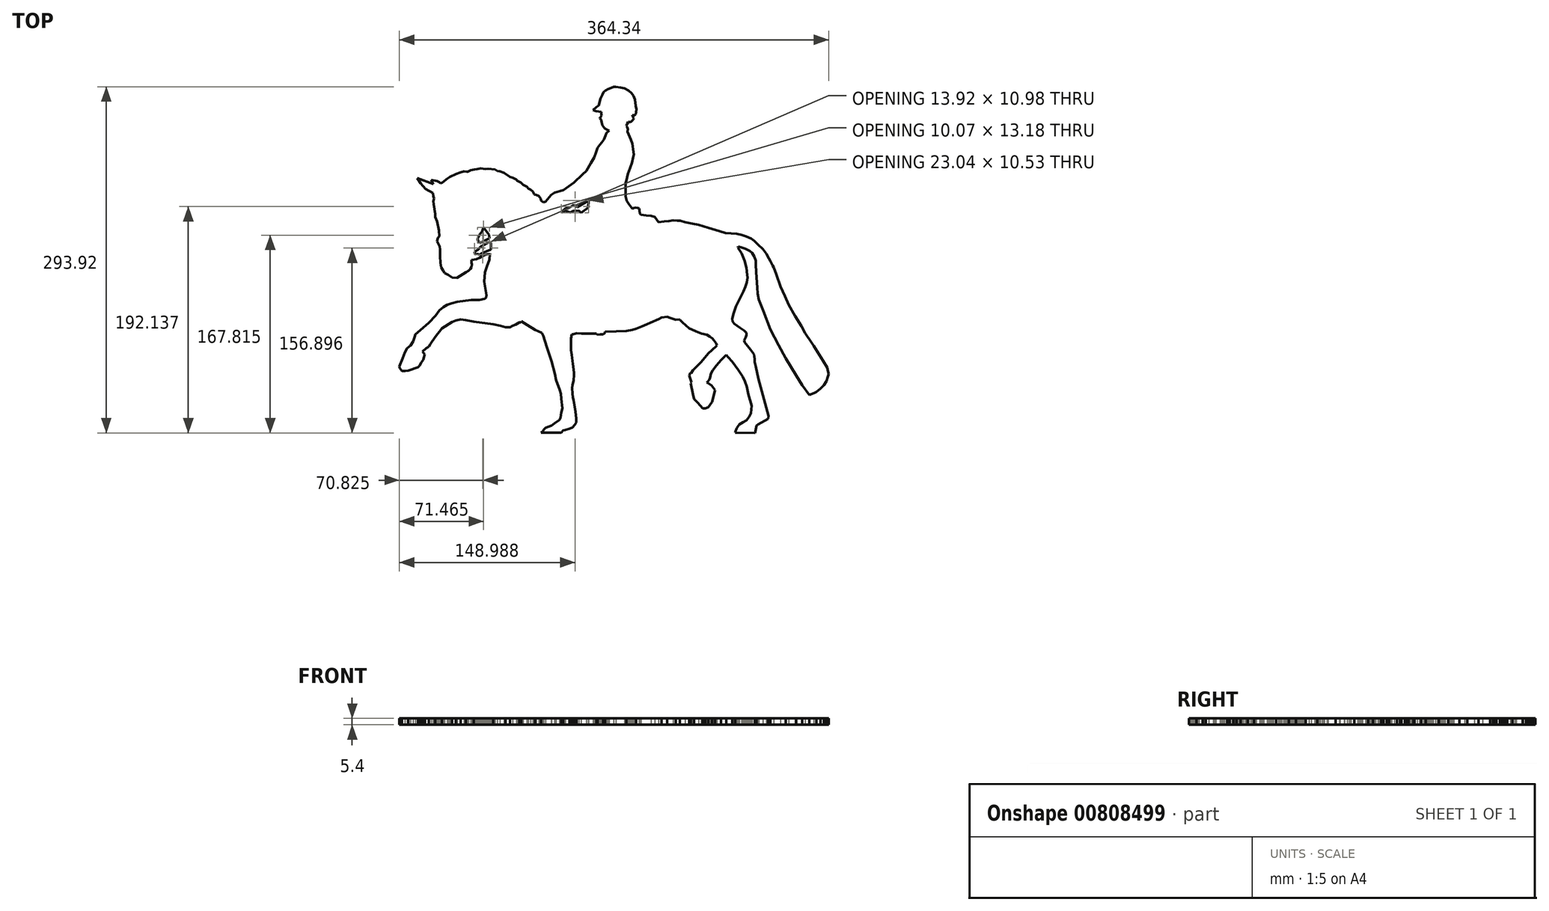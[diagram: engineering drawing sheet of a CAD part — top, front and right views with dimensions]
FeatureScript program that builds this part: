
annotation { "Feature Type Name" : "Feature", "Feature Type Description" : "" }
export const myFeature = defineFeature(function(context is Context, id is Id, definition is map)
    precondition{}
    {
        {
            var Q0;
            Q0=qCreatedBy(makeId("Top.planeOp"),FACE);
            var sketch = newSketch(context, id + "F0", { "sketchPlane" : qUnion([Q0])});
            skLineSegment(sketch, "E0", {"start": v(-15.37, 154) * mm, "end": v(-13.56, 161.2) * mm});
            skLineSegment(sketch, "E1", {"start": v(-13.56, 161.2) * mm, "end": v(-11.74, 164.95) * mm});
            skLineSegment(sketch, "E2", {"start": v(-11.74, 164.95) * mm, "end": v(-10.33, 167.52) * mm});
            skLineSegment(sketch, "E3", {"start": v(-10.33, 167.52) * mm, "end": v(-8.43, 168.95) * mm});
            skLineSegment(sketch, "E4", {"start": v(-8.43, 168.95) * mm, "end": v(-6.07, 170.71) * mm});
            skLineSegment(sketch, "E5", {"start": v(-6.07, 170.71) * mm, "end": v(-3.07, 171.86) * mm});
            skLineSegment(sketch, "E6", {"start": v(-3.07, 171.86) * mm, "end": v(-0.38, 172.9) * mm});
            skLineSegment(sketch, "E7", {"start": v(-0.38, 172.9) * mm, "end": v(1.87, 172.9) * mm});
            skLineSegment(sketch, "E8", {"start": v(1.87, 172.9) * mm, "end": v(6.63, 171.98) * mm});
            skLineSegment(sketch, "E9", {"start": v(6.63, 171.98) * mm, "end": v(10.5, 171.24) * mm});
            skLineSegment(sketch, "E10", {"start": v(10.5, 171.24) * mm, "end": v(14.63, 169.07) * mm});
            skLineSegment(sketch, "E11", {"start": v(14.63, 169.07) * mm, "end": v(17.67, 166.4) * mm});
            skLineSegment(sketch, "E12", {"start": v(17.67, 166.4) * mm, "end": v(19.46, 163.77) * mm});
            skLineSegment(sketch, "E13", {"start": v(19.46, 163.77) * mm, "end": v(20.82, 160.15) * mm});
            skLineSegment(sketch, "E14", {"start": v(20.82, 160.15) * mm, "end": v(21.78, 153.95) * mm});
            skLineSegment(sketch, "E15", {"start": v(21.78, 153.95) * mm, "end": v(22.35, 150.26) * mm});
            skLineSegment(sketch, "E16", {"start": v(22.35, 150.26) * mm, "end": v(21.66, 145.02) * mm});
            skLineSegment(sketch, "E17", {"start": v(21.66, 145.02) * mm, "end": v(20.23, 144.3) * mm});
            skLineSegment(sketch, "E18", {"start": v(20.23, 144.3) * mm, "end": v(18.45, 144.3) * mm});
            skLineSegment(sketch, "E19", {"start": v(18.45, 144.3) * mm, "end": v(18.45, 143.54) * mm});
            skLineSegment(sketch, "E20", {"start": v(18.45, 143.54) * mm, "end": v(19.7, 141.63) * mm});
            skLineSegment(sketch, "E21", {"start": v(19.7, 141.63) * mm, "end": v(18.86, 139.85) * mm});
            skLineSegment(sketch, "E22", {"start": v(18.86, 139.85) * mm, "end": v(17.08, 138) * mm});
            skLineSegment(sketch, "E23", {"start": v(17.08, 138) * mm, "end": v(16.05, 137.61) * mm});
            skLineSegment(sketch, "E24", {"start": v(16.05, 137.61) * mm, "end": v(14.06, 137.61) * mm});
            skLineSegment(sketch, "E25", {"start": v(14.06, 137.61) * mm, "end": v(13.19, 135.72) * mm});
            skLineSegment(sketch, "E26", {"start": v(13.19, 135.72) * mm, "end": v(12.47, 134.16) * mm});
            skLineSegment(sketch, "E27", {"start": v(12.47, 134.16) * mm, "end": v(13.23, 133) * mm});
            skLineSegment(sketch, "E28", {"start": v(13.23, 133) * mm, "end": v(13.7, 130.65) * mm});
            skLineSegment(sketch, "E29", {"start": v(13.7, 130.65) * mm, "end": v(13.45, 127.94) * mm});
            skLineSegment(sketch, "E30", {"start": v(13.45, 127.94) * mm, "end": v(14.48, 125.44) * mm});
            skLineSegment(sketch, "E31", {"start": v(14.48, 125.44) * mm, "end": v(16.64, 120.14) * mm});
            skLineSegment(sketch, "E32", {"start": v(16.64, 120.14) * mm, "end": v(18.28, 116.14) * mm});
            skLineSegment(sketch, "E33", {"start": v(18.28, 116.14) * mm, "end": v(18.93, 111.56) * mm});
            skLineSegment(sketch, "E34", {"start": v(18.93, 111.56) * mm, "end": v(19.48, 107.66) * mm});
            skLineSegment(sketch, "E35", {"start": v(19.48, 107.66) * mm, "end": v(19.84, 105.1) * mm});
            skLineSegment(sketch, "E36", {"start": v(19.84, 105.1) * mm, "end": v(19.12, 102.22) * mm});
            skLineSegment(sketch, "E37", {"start": v(19.12, 102.22) * mm, "end": v(17.84, 97.06) * mm});
            skLineSegment(sketch, "E38", {"start": v(17.84, 97.06) * mm, "end": v(15.94, 91.85) * mm});
            skLineSegment(sketch, "E39", {"start": v(15.94, 91.85) * mm, "end": v(13.76, 85.9) * mm});
            skLineSegment(sketch, "E40", {"start": v(13.76, 85.9) * mm, "end": v(12.23, 79.26) * mm});
            skLineSegment(sketch, "E41", {"start": v(12.23, 79.26) * mm, "end": v(11.64, 76.7) * mm});
            skLineSegment(sketch, "E42", {"start": v(11.64, 76.7) * mm, "end": v(11.64, 68.11) * mm});
            skLineSegment(sketch, "E43", {"start": v(11.64, 68.11) * mm, "end": v(11.64, 66.83) * mm});
            skLineSegment(sketch, "E44", {"start": v(11.64, 66.83) * mm, "end": v(11.64, 63.5) * mm});
            skLineSegment(sketch, "E45", {"start": v(11.64, 63.5) * mm, "end": v(12.53, 59.03) * mm});
            skLineSegment(sketch, "E46", {"start": v(12.53, 59.03) * mm, "end": v(14.96, 55.61) * mm});
            skLineSegment(sketch, "E47", {"start": v(14.96, 55.61) * mm, "end": v(18.15, 51.12) * mm});
            skLineSegment(sketch, "E48", {"start": v(18.15, 51.12) * mm, "end": v(19.88, 51.64) * mm});
            skLineSegment(sketch, "E49", {"start": v(19.88, 51.64) * mm, "end": v(21.8, 52.22) * mm});
            skLineSegment(sketch, "E50", {"start": v(21.8, 52.22) * mm, "end": v(23.75, 51.69) * mm});
            skLineSegment(sketch, "E51", {"start": v(23.75, 51.69) * mm, "end": v(25.12, 51.32) * mm});
            skLineSegment(sketch, "E52", {"start": v(25.12, 51.32) * mm, "end": v(25.29, 49.75) * mm});
            skLineSegment(sketch, "E53", {"start": v(25.29, 49.75) * mm, "end": v(25.65, 46.4) * mm});
            skLineSegment(sketch, "E54", {"start": v(25.65, 46.4) * mm, "end": v(26.93, 45.03) * mm});
            skLineSegment(sketch, "E55", {"start": v(26.93, 45.03) * mm, "end": v(31.94, 44.43) * mm});
            skLineSegment(sketch, "E56", {"start": v(31.94, 44.43) * mm, "end": v(37.06, 43.83) * mm});
            skLineSegment(sketch, "E57", {"start": v(37.06, 43.83) * mm, "end": v(40.68, 42.7) * mm});
            skLineSegment(sketch, "E58", {"start": v(40.68, 42.7) * mm, "end": v(42.57, 40.2) * mm});
            skLineSegment(sketch, "E59", {"start": v(42.57, 40.2) * mm, "end": v(44.49, 37.67) * mm});
            skLineSegment(sketch, "E60", {"start": v(44.49, 37.67) * mm, "end": v(50.12, 38.31) * mm});
            skLineSegment(sketch, "E61", {"start": v(50.12, 38.31) * mm, "end": v(54.89, 38.86) * mm});
            skLineSegment(sketch, "E62", {"start": v(54.89, 38.86) * mm, "end": v(58.92, 39.32) * mm});
            skLineSegment(sketch, "E63", {"start": v(58.92, 39.32) * mm, "end": v(63.15, 39.2) * mm});
            skLineSegment(sketch, "E64", {"start": v(63.15, 39.2) * mm, "end": v(66.23, 39.12) * mm});
            skLineSegment(sketch, "E65", {"start": v(66.23, 39.12) * mm, "end": v(71, 37.71) * mm});
            skLineSegment(sketch, "E66", {"start": v(71, 37.71) * mm, "end": v(78.25, 36.22) * mm});
            skLineSegment(sketch, "E67", {"start": v(78.25, 36.22) * mm, "end": v(84.31, 34.97) * mm});
            skLineSegment(sketch, "E68", {"start": v(84.31, 34.97) * mm, "end": v(94, 32.04) * mm});
            skLineSegment(sketch, "E69", {"start": v(94, 32.04) * mm, "end": v(105.26, 28.65) * mm});
            skLineSegment(sketch, "E70", {"start": v(105.26, 28.65) * mm, "end": v(111.22, 26.85) * mm});
            skLineSegment(sketch, "E71", {"start": v(111.22, 26.85) * mm, "end": v(116.82, 26.42) * mm});
            skLineSegment(sketch, "E72", {"start": v(116.82, 26.42) * mm, "end": v(122.43, 26) * mm});
            skLineSegment(sketch, "E73", {"start": v(122.43, 26) * mm, "end": v(127.42, 24.88) * mm});
            skLineSegment(sketch, "E74", {"start": v(127.42, 24.88) * mm, "end": v(131.84, 23.24) * mm});
            skLineSegment(sketch, "E75", {"start": v(131.84, 23.24) * mm, "end": v(137.18, 21.26) * mm});
            skLineSegment(sketch, "E76", {"start": v(137.18, 21.26) * mm, "end": v(140.13, 19.07) * mm});
            skLineSegment(sketch, "E77", {"start": v(140.13, 19.07) * mm, "end": v(143.87, 15.4) * mm});
            skLineSegment(sketch, "E78", {"start": v(143.87, 15.4) * mm, "end": v(148.55, 10.79) * mm});
            skLineSegment(sketch, "E79", {"start": v(148.55, 10.79) * mm, "end": v(151.92, 6.2) * mm});
            skLineSegment(sketch, "E80", {"start": v(151.92, 6.2) * mm, "end": v(154.55, 1.43) * mm});
            skLineSegment(sketch, "E81", {"start": v(154.55, 1.43) * mm, "end": v(156.03, -1.24) * mm});
            skLineSegment(sketch, "E82", {"start": v(156.03, -1.24) * mm, "end": v(158.45, -5.64) * mm});
            skLineSegment(sketch, "E83", {"start": v(158.45, -5.64) * mm, "end": v(159.57, -7.67) * mm});
            skLineSegment(sketch, "E84", {"start": v(159.57, -7.67) * mm, "end": v(162, -14.62) * mm});
            skLineSegment(sketch, "E85", {"start": v(162, -14.62) * mm, "end": v(166.17, -26.5) * mm});
            skLineSegment(sketch, "E86", {"start": v(166.17, -26.5) * mm, "end": v(170.5, -36.2) * mm});
            skLineSegment(sketch, "E87", {"start": v(170.5, -36.2) * mm, "end": v(174.36, -44.8) * mm});
            skLineSegment(sketch, "E88", {"start": v(174.36, -44.8) * mm, "end": v(180.75, -56.32) * mm});
            skLineSegment(sketch, "E89", {"start": v(180.75, -56.32) * mm, "end": v(187, -66.21) * mm});
            skLineSegment(sketch, "E90", {"start": v(187, -66.21) * mm, "end": v(191.02, -73.19) * mm});
            skLineSegment(sketch, "E91", {"start": v(191.02, -73.19) * mm, "end": v(197.28, -82.58) * mm});
            skLineSegment(sketch, "E92", {"start": v(197.28, -82.58) * mm, "end": v(199.58, -86.03) * mm});
            skLineSegment(sketch, "E93", {"start": v(199.58, -86.03) * mm, "end": v(208.64, -100.87) * mm});
            skLineSegment(sketch, "E94", {"start": v(208.64, -100.87) * mm, "end": v(212.88, -107.8) * mm});
            skLineSegment(sketch, "E95", {"start": v(212.88, -107.8) * mm, "end": v(213.74, -111.58) * mm});
            skLineSegment(sketch, "E96", {"start": v(213.74, -111.58) * mm, "end": v(214.31, -114.1) * mm});
            skLineSegment(sketch, "E97", {"start": v(214.31, -114.1) * mm, "end": v(213.22, -117.4) * mm});
            skLineSegment(sketch, "E98", {"start": v(213.22, -117.4) * mm, "end": v(211.97, -121.16) * mm});
            skLineSegment(sketch, "E99", {"start": v(211.97, -121.16) * mm, "end": v(209.44, -125.28) * mm});
            skLineSegment(sketch, "E100", {"start": v(209.44, -125.28) * mm, "end": v(206.32, -128.57) * mm});
            skLineSegment(sketch, "E101", {"start": v(206.32, -128.57) * mm, "end": v(202.14, -132.05) * mm});
            skLineSegment(sketch, "E102", {"start": v(202.14, -132.05) * mm, "end": v(199.85, -132.94) * mm});
            skLineSegment(sketch, "E103", {"start": v(199.85, -132.94) * mm, "end": v(194.97, -134.81) * mm});
            skLineSegment(sketch, "E104", {"start": v(194.97, -134.81) * mm, "end": v(187.9, -125.23) * mm});
            skLineSegment(sketch, "E105", {"start": v(187.9, -125.23) * mm, "end": v(181.73, -115.6) * mm});
            skLineSegment(sketch, "E106", {"start": v(181.73, -115.6) * mm, "end": v(171.37, -98.23) * mm});
            skLineSegment(sketch, "E107", {"start": v(171.37, -98.23) * mm, "end": v(164.42, -85.16) * mm});
            skLineSegment(sketch, "E108", {"start": v(164.42, -85.16) * mm, "end": v(156.13, -69.55) * mm});
            skLineSegment(sketch, "E109", {"start": v(156.13, -69.55) * mm, "end": v(148.82, -51.07) * mm});
            skLineSegment(sketch, "E110", {"start": v(148.82, -51.07) * mm, "end": v(144.38, -39.85) * mm});
            skLineSegment(sketch, "E111", {"start": v(144.38, -39.85) * mm, "end": v(143.29, -33.88) * mm});
            skLineSegment(sketch, "E112", {"start": v(143.29, -33.88) * mm, "end": v(142.93, -27.82) * mm});
            skLineSegment(sketch, "E113", {"start": v(142.93, -27.82) * mm, "end": v(142.04, -12.48) * mm});
            skLineSegment(sketch, "E114", {"start": v(142.04, -12.48) * mm, "end": v(141.59, -4.76) * mm});
            skLineSegment(sketch, "E115", {"start": v(141.59, -4.76) * mm, "end": v(141.37, -0.93) * mm});
            skLineSegment(sketch, "E116", {"start": v(141.37, -0.93) * mm, "end": v(140.11, 3.27) * mm});
            skLineSegment(sketch, "E117", {"start": v(140.11, 3.27) * mm, "end": v(137.82, 7.09) * mm});
            skLineSegment(sketch, "E118", {"start": v(137.82, 7.09) * mm, "end": v(135.57, 8.99) * mm});
            skLineSegment(sketch, "E119", {"start": v(135.57, 8.99) * mm, "end": v(130.99, 11.28) * mm});
            skLineSegment(sketch, "E120", {"start": v(130.99, 11.28) * mm, "end": v(126.7, 12.63) * mm});
            skLineSegment(sketch, "E121", {"start": v(126.7, 12.63) * mm, "end": v(124.1, 13.45) * mm});
            skLineSegment(sketch, "E122", {"start": v(124.1, 13.45) * mm, "end": v(123.63, 12.16) * mm});
            skLineSegment(sketch, "E123", {"start": v(123.63, 12.16) * mm, "end": v(125.05, 10.1) * mm});
            skLineSegment(sketch, "E124", {"start": v(125.05, 10.1) * mm, "end": v(127.45, 6.6) * mm});
            skLineSegment(sketch, "E125", {"start": v(127.45, 6.6) * mm, "end": v(128.99, 2.87) * mm});
            skLineSegment(sketch, "E126", {"start": v(128.99, 2.87) * mm, "end": v(130.5, -0.81) * mm});
            skLineSegment(sketch, "E127", {"start": v(130.5, -0.81) * mm, "end": v(132.22, -7.94) * mm});
            skLineSegment(sketch, "E128", {"start": v(132.22, -7.94) * mm, "end": v(133.05, -14.95) * mm});
            skLineSegment(sketch, "E129", {"start": v(133.05, -14.95) * mm, "end": v(133.36, -17.62) * mm});
            skLineSegment(sketch, "E130", {"start": v(133.36, -17.62) * mm, "end": v(132.75, -22.6) * mm});
            skLineSegment(sketch, "E131", {"start": v(132.75, -22.6) * mm, "end": v(131.22, -27.13) * mm});
            skLineSegment(sketch, "E132", {"start": v(131.22, -27.13) * mm, "end": v(129.1, -31.42) * mm});
            skLineSegment(sketch, "E133", {"start": v(129.1, -31.42) * mm, "end": v(124.58, -40.6) * mm});
            skLineSegment(sketch, "E134", {"start": v(124.58, -40.6) * mm, "end": v(121.74, -46.35) * mm});
            skLineSegment(sketch, "E135", {"start": v(121.74, -46.35) * mm, "end": v(119.4, -52.99) * mm});
            skLineSegment(sketch, "E136", {"start": v(119.4, -52.99) * mm, "end": v(118.1, -58.57) * mm});
            skLineSegment(sketch, "E137", {"start": v(118.1, -58.57) * mm, "end": v(118.33, -61.75) * mm});
            skLineSegment(sketch, "E138", {"start": v(118.33, -61.75) * mm, "end": v(120.16, -64.16) * mm});
            skLineSegment(sketch, "E139", {"start": v(120.16, -64.16) * mm, "end": v(125.63, -67.71) * mm});
            skLineSegment(sketch, "E140", {"start": v(125.63, -67.71) * mm, "end": v(129.97, -70.52) * mm});
            skLineSegment(sketch, "E141", {"start": v(129.97, -70.52) * mm, "end": v(132.04, -72.94) * mm});
            skLineSegment(sketch, "E142", {"start": v(132.04, -72.94) * mm, "end": v(132.34, -75.24) * mm});
            skLineSegment(sketch, "E143", {"start": v(132.34, -75.24) * mm, "end": v(131.28, -77.53) * mm});
            skLineSegment(sketch, "E144", {"start": v(131.28, -77.53) * mm, "end": v(130.02, -80.26) * mm});
            skLineSegment(sketch, "E145", {"start": v(130.02, -80.26) * mm, "end": v(130.4, -82.25) * mm});
            skLineSegment(sketch, "E146", {"start": v(130.4, -82.25) * mm, "end": v(136.34, -89.84) * mm});
            skLineSegment(sketch, "E147", {"start": v(136.34, -89.84) * mm, "end": v(139.78, -94.23) * mm});
            skLineSegment(sketch, "E148", {"start": v(139.78, -94.23) * mm, "end": v(140.16, -96.48) * mm});
            skLineSegment(sketch, "E149", {"start": v(140.16, -96.48) * mm, "end": v(140.6, -99) * mm});
            skLineSegment(sketch, "E150", {"start": v(140.6, -99) * mm, "end": v(140.4, -102.03) * mm});
            skLineSegment(sketch, "E151", {"start": v(140.4, -102.03) * mm, "end": v(141.4, -106.38) * mm});
            skLineSegment(sketch, "E152", {"start": v(141.4, -106.38) * mm, "end": v(144.26, -118.83) * mm});
            skLineSegment(sketch, "E153", {"start": v(144.26, -118.83) * mm, "end": v(148.7, -135.34) * mm});
            skLineSegment(sketch, "E154", {"start": v(148.7, -135.34) * mm, "end": v(152.32, -148.84) * mm});
            skLineSegment(sketch, "E155", {"start": v(152.32, -148.84) * mm, "end": v(154.25, -156) * mm});
            skLineSegment(sketch, "E156", {"start": v(154.25, -156) * mm, "end": v(153.94, -158.96) * mm});
            skLineSegment(sketch, "E157", {"start": v(153.94, -158.96) * mm, "end": v(143.88, -164.55) * mm});
            skLineSegment(sketch, "E158", {"start": v(143.88, -164.55) * mm, "end": v(142.23, -165.47) * mm});
            skLineSegment(sketch, "E159", {"start": v(142.23, -165.47) * mm, "end": v(141.65, -168.66) * mm});
            skLineSegment(sketch, "E160", {"start": v(141.65, -168.66) * mm, "end": v(140.88, -172.9) * mm});
            skLineSegment(sketch, "E161", {"start": v(140.88, -172.9) * mm, "end": v(120.98, -172.74) * mm});
            skLineSegment(sketch, "E162", {"start": v(120.98, -172.74) * mm, "end": v(121.45, -171.15) * mm});
            skLineSegment(sketch, "E163", {"start": v(121.45, -171.15) * mm, "end": v(122.31, -168.25) * mm});
            skLineSegment(sketch, "E164", {"start": v(122.31, -168.25) * mm, "end": v(124.04, -165.86) * mm});
            skLineSegment(sketch, "E165", {"start": v(124.04, -165.86) * mm, "end": v(125.1, -164.4) * mm});
            skLineSegment(sketch, "E166", {"start": v(125.1, -164.4) * mm, "end": v(128.8, -162.28) * mm});
            skLineSegment(sketch, "E167", {"start": v(128.8, -162.28) * mm, "end": v(132.28, -160.28) * mm});
            skLineSegment(sketch, "E168", {"start": v(132.28, -160.28) * mm, "end": v(134.8, -157.04) * mm});
            skLineSegment(sketch, "E169", {"start": v(134.8, -157.04) * mm, "end": v(136.63, -153.16) * mm});
            skLineSegment(sketch, "E170", {"start": v(136.63, -153.16) * mm, "end": v(137.04, -149.7) * mm});
            skLineSegment(sketch, "E171", {"start": v(137.04, -149.7) * mm, "end": v(137.49, -145.93) * mm});
            skLineSegment(sketch, "E172", {"start": v(137.49, -145.93) * mm, "end": v(133.92, -134.1) * mm});
            skLineSegment(sketch, "E173", {"start": v(133.92, -134.1) * mm, "end": v(132.74, -126.6) * mm});
            skLineSegment(sketch, "E174", {"start": v(132.74, -126.6) * mm, "end": v(130.8, -121.43) * mm});
            skLineSegment(sketch, "E175", {"start": v(130.8, -121.43) * mm, "end": v(128.33, -116.78) * mm});
            skLineSegment(sketch, "E176", {"start": v(128.33, -116.78) * mm, "end": v(123.8, -110.01) * mm});
            skLineSegment(sketch, "E177", {"start": v(123.8, -110.01) * mm, "end": v(118.14, -101.57) * mm});
            skLineSegment(sketch, "E178", {"start": v(118.14, -101.57) * mm, "end": v(114.02, -97.18) * mm});
            skLineSegment(sketch, "E179", {"start": v(114.02, -97.18) * mm, "end": v(111.93, -94.95) * mm});
            skLineSegment(sketch, "E180", {"start": v(111.93, -94.95) * mm, "end": v(106.73, -100.05) * mm});
            skLineSegment(sketch, "E181", {"start": v(106.73, -100.05) * mm, "end": v(102.5, -105.4) * mm});
            skLineSegment(sketch, "E182", {"start": v(102.5, -105.4) * mm, "end": v(98.67, -110.22) * mm});
            skLineSegment(sketch, "E183", {"start": v(98.67, -110.22) * mm, "end": v(96.79, -113.8) * mm});
            skLineSegment(sketch, "E184", {"start": v(96.79, -113.8) * mm, "end": v(95.9, -117.4) * mm});
            skLineSegment(sketch, "E185", {"start": v(95.9, -117.4) * mm, "end": v(95.33, -119.72) * mm});
            skLineSegment(sketch, "E186", {"start": v(95.33, -119.72) * mm, "end": v(93.38, -121.92) * mm});
            skLineSegment(sketch, "E187", {"start": v(93.38, -121.92) * mm, "end": v(92.71, -122.66) * mm});
            skLineSegment(sketch, "E188", {"start": v(92.71, -122.66) * mm, "end": v(93.67, -123.1) * mm});
            skLineSegment(sketch, "E189", {"start": v(93.67, -123.1) * mm, "end": v(97.32, -125.63) * mm});
            skLineSegment(sketch, "E190", {"start": v(97.32, -125.63) * mm, "end": v(99.61, -128.52) * mm});
            skLineSegment(sketch, "E191", {"start": v(99.61, -128.52) * mm, "end": v(100.78, -129.98) * mm});
            skLineSegment(sketch, "E192", {"start": v(100.78, -129.98) * mm, "end": v(98.5, -139.47) * mm});
            skLineSegment(sketch, "E193", {"start": v(98.5, -139.47) * mm, "end": v(97.92, -141.87) * mm});
            skLineSegment(sketch, "E194", {"start": v(97.92, -141.87) * mm, "end": v(95.9, -144.72) * mm});
            skLineSegment(sketch, "E195", {"start": v(95.9, -144.72) * mm, "end": v(93.95, -147.46) * mm});
            skLineSegment(sketch, "E196", {"start": v(93.95, -147.46) * mm, "end": v(91.07, -148.36) * mm});
            skLineSegment(sketch, "E197", {"start": v(91.07, -148.36) * mm, "end": v(88.54, -148.3) * mm});
            skLineSegment(sketch, "E198", {"start": v(88.54, -148.3) * mm, "end": v(86.19, -145.77) * mm});
            skLineSegment(sketch, "E199", {"start": v(86.19, -145.77) * mm, "end": v(83.23, -142.6) * mm});
            skLineSegment(sketch, "E200", {"start": v(83.23, -142.6) * mm, "end": v(81.22, -140.42) * mm});
            skLineSegment(sketch, "E201", {"start": v(81.22, -140.42) * mm, "end": v(80.8, -139.99) * mm});
            skLineSegment(sketch, "E202", {"start": v(80.8, -139.99) * mm, "end": v(79.96, -139.08) * mm});
            skLineSegment(sketch, "E203", {"start": v(79.96, -139.08) * mm, "end": v(78.88, -134.06) * mm});
            skLineSegment(sketch, "E204", {"start": v(78.88, -134.06) * mm, "end": v(76.6, -123.46) * mm});
            skLineSegment(sketch, "E205", {"start": v(76.6, -123.46) * mm, "end": v(77.12, -122.25) * mm});
            skLineSegment(sketch, "E206", {"start": v(77.12, -122.25) * mm, "end": v(75.18, -115.66) * mm});
            skLineSegment(sketch, "E207", {"start": v(75.18, -115.66) * mm, "end": v(75.65, -114.13) * mm});
            skLineSegment(sketch, "E208", {"start": v(75.65, -114.13) * mm, "end": v(75.98, -113.05) * mm});
            skLineSegment(sketch, "E209", {"start": v(75.98, -113.05) * mm, "end": v(76.83, -113.13) * mm});
            skLineSegment(sketch, "E210", {"start": v(76.83, -113.13) * mm, "end": v(78.94, -110.31) * mm});
            skLineSegment(sketch, "E211", {"start": v(78.94, -110.31) * mm, "end": v(86.95, -102.12) * mm});
            skLineSegment(sketch, "E212", {"start": v(86.95, -102.12) * mm, "end": v(94.24, -93.65) * mm});
            skLineSegment(sketch, "E213", {"start": v(94.24, -93.65) * mm, "end": v(101.78, -86.28) * mm});
            skLineSegment(sketch, "E214", {"start": v(101.78, -86.28) * mm, "end": v(102.67, -85.4) * mm});
            skLineSegment(sketch, "E215", {"start": v(102.67, -85.4) * mm, "end": v(101.95, -83.51) * mm});
            skLineSegment(sketch, "E216", {"start": v(101.95, -83.51) * mm, "end": v(99.78, -80.52) * mm});
            skLineSegment(sketch, "E217", {"start": v(99.78, -80.52) * mm, "end": v(98.27, -78.44) * mm});
            skLineSegment(sketch, "E218", {"start": v(98.27, -78.44) * mm, "end": v(95.42, -76.68) * mm});
            skLineSegment(sketch, "E219", {"start": v(95.42, -76.68) * mm, "end": v(92.65, -74.98) * mm});
            skLineSegment(sketch, "E220", {"start": v(92.65, -74.98) * mm, "end": v(87.24, -73.68) * mm});
            skLineSegment(sketch, "E221", {"start": v(87.24, -73.68) * mm, "end": v(81.89, -71.45) * mm});
            skLineSegment(sketch, "E222", {"start": v(81.89, -71.45) * mm, "end": v(77.64, -69.67) * mm});
            skLineSegment(sketch, "E223", {"start": v(77.64, -69.67) * mm, "end": v(74.96, -68.56) * mm});
            skLineSegment(sketch, "E224", {"start": v(74.96, -68.56) * mm, "end": v(68.4, -62.32) * mm});
            skLineSegment(sketch, "E225", {"start": v(68.4, -62.32) * mm, "end": v(66.26, -60.27) * mm});
            skLineSegment(sketch, "E226", {"start": v(66.26, -60.27) * mm, "end": v(65.57, -59.62) * mm});
            skLineSegment(sketch, "E227", {"start": v(65.57, -59.62) * mm, "end": v(61.7, -59.84) * mm});
            skLineSegment(sketch, "E228", {"start": v(61.7, -59.84) * mm, "end": v(55.87, -57.85) * mm});
            skLineSegment(sketch, "E229", {"start": v(55.87, -57.85) * mm, "end": v(53.16, -56.91) * mm});
            skLineSegment(sketch, "E230", {"start": v(53.16, -56.91) * mm, "end": v(47.57, -57.78) * mm});
            skLineSegment(sketch, "E231", {"start": v(47.57, -57.78) * mm, "end": v(44.63, -59.07) * mm});
            skLineSegment(sketch, "E232", {"start": v(44.63, -59.07) * mm, "end": v(36.37, -62.7) * mm});
            skLineSegment(sketch, "E233", {"start": v(36.37, -62.7) * mm, "end": v(32.94, -64.21) * mm});
            skLineSegment(sketch, "E234", {"start": v(32.94, -64.21) * mm, "end": v(27.77, -66.49) * mm});
            skLineSegment(sketch, "E235", {"start": v(27.77, -66.49) * mm, "end": v(22.08, -68.99) * mm});
            skLineSegment(sketch, "E236", {"start": v(22.08, -68.99) * mm, "end": v(18.2, -69.84) * mm});
            skLineSegment(sketch, "E237", {"start": v(18.2, -69.84) * mm, "end": v(12.42, -71.11) * mm});
            skLineSegment(sketch, "E238", {"start": v(12.42, -71.11) * mm, "end": v(2.3, -71.5) * mm});
            skLineSegment(sketch, "E239", {"start": v(2.3, -71.5) * mm, "end": v(-9.07, -71.92) * mm});
            skLineSegment(sketch, "E240", {"start": v(-9.07, -71.92) * mm, "end": v(-9.37, -73.5) * mm});
            skLineSegment(sketch, "E241", {"start": v(-9.37, -73.5) * mm, "end": v(-10.9, -74.38) * mm});
            skLineSegment(sketch, "E242", {"start": v(-10.9, -74.38) * mm, "end": v(-13.72, -74.61) * mm});
            skLineSegment(sketch, "E243", {"start": v(-13.72, -74.61) * mm, "end": v(-16.46, -74.84) * mm});
            skLineSegment(sketch, "E244", {"start": v(-16.46, -74.84) * mm, "end": v(-17.49, -74.02) * mm});
            skLineSegment(sketch, "E245", {"start": v(-17.49, -74.02) * mm, "end": v(-17.73, -73.83) * mm});
            skLineSegment(sketch, "E246", {"start": v(-17.73, -73.83) * mm, "end": v(-28.15, -73.61) * mm});
            skLineSegment(sketch, "E247", {"start": v(-28.15, -73.61) * mm, "end": v(-32.67, -73.51) * mm});
            skLineSegment(sketch, "E248", {"start": v(-32.67, -73.51) * mm, "end": v(-37.34, -73.41) * mm});
            skLineSegment(sketch, "E249", {"start": v(-37.34, -73.41) * mm, "end": v(-41.1, -74.32) * mm});
            skLineSegment(sketch, "E250", {"start": v(-41.1, -74.32) * mm, "end": v(-42.26, -74.59) * mm});
            skLineSegment(sketch, "E251", {"start": v(-42.26, -74.59) * mm, "end": v(-42.87, -78.43) * mm});
            skLineSegment(sketch, "E252", {"start": v(-42.87, -78.43) * mm, "end": v(-42.93, -84.96) * mm});
            skLineSegment(sketch, "E253", {"start": v(-42.93, -84.96) * mm, "end": v(-42.97, -89.95) * mm});
            skLineSegment(sketch, "E254", {"start": v(-42.97, -89.95) * mm, "end": v(-42.34, -94.9) * mm});
            skLineSegment(sketch, "E255", {"start": v(-42.34, -94.9) * mm, "end": v(-41.2, -103.76) * mm});
            skLineSegment(sketch, "E256", {"start": v(-41.2, -103.76) * mm, "end": v(-40.07, -112.66) * mm});
            skLineSegment(sketch, "E257", {"start": v(-40.07, -112.66) * mm, "end": v(-39.8, -114.7) * mm});
            skLineSegment(sketch, "E258", {"start": v(-39.8, -114.7) * mm, "end": v(-40.28, -120.92) * mm});
            skLineSegment(sketch, "E259", {"start": v(-40.28, -120.92) * mm, "end": v(-41.58, -125.04) * mm});
            skLineSegment(sketch, "E260", {"start": v(-41.58, -125.04) * mm, "end": v(-41.75, -128.3) * mm});
            skLineSegment(sketch, "E261", {"start": v(-41.75, -128.3) * mm, "end": v(-41.4, -133.4) * mm});
            skLineSegment(sketch, "E262", {"start": v(-41.4, -133.4) * mm, "end": v(-41.11, -137.55) * mm});
            skLineSegment(sketch, "E263", {"start": v(-41.11, -137.55) * mm, "end": v(-40.22, -140.28) * mm});
            skLineSegment(sketch, "E264", {"start": v(-40.22, -140.28) * mm, "end": v(-38.57, -151.88) * mm});
            skLineSegment(sketch, "E265", {"start": v(-38.57, -151.88) * mm, "end": v(-37.63, -158.51) * mm});
            skLineSegment(sketch, "E266", {"start": v(-37.63, -158.51) * mm, "end": v(-37.92, -162.66) * mm});
            skLineSegment(sketch, "E267", {"start": v(-37.92, -162.66) * mm, "end": v(-39.22, -164.84) * mm});
            skLineSegment(sketch, "E268", {"start": v(-39.22, -164.84) * mm, "end": v(-41.57, -167.26) * mm});
            skLineSegment(sketch, "E269", {"start": v(-41.57, -167.26) * mm, "end": v(-44.16, -168.44) * mm});
            skLineSegment(sketch, "E270", {"start": v(-44.16, -168.44) * mm, "end": v(-49.05, -169.92) * mm});
            skLineSegment(sketch, "E271", {"start": v(-49.05, -169.92) * mm, "end": v(-51.01, -170.5) * mm});
            skLineSegment(sketch, "E272", {"start": v(-51.01, -170.5) * mm, "end": v(-52.58, -172.8) * mm});
            skLineSegment(sketch, "E273", {"start": v(-52.58, -172.8) * mm, "end": v(-72.84, -172.74) * mm});
            skLineSegment(sketch, "E274", {"start": v(-72.84, -172.74) * mm, "end": v(-72.19, -171.92) * mm});
            skLineSegment(sketch, "E275", {"start": v(-72.19, -171.92) * mm, "end": v(-70.84, -171.21) * mm});
            skLineSegment(sketch, "E276", {"start": v(-70.84, -171.21) * mm, "end": v(-70.07, -169.8) * mm});
            skLineSegment(sketch, "E277", {"start": v(-70.07, -169.8) * mm, "end": v(-68.19, -167.86) * mm});
            skLineSegment(sketch, "E278", {"start": v(-68.19, -167.86) * mm, "end": v(-65.48, -166.69) * mm});
            skLineSegment(sketch, "E279", {"start": v(-65.48, -166.69) * mm, "end": v(-62.58, -165.42) * mm});
            skLineSegment(sketch, "E280", {"start": v(-62.58, -165.42) * mm, "end": v(-59.6, -163.45) * mm});
            skLineSegment(sketch, "E281", {"start": v(-59.6, -163.45) * mm, "end": v(-57.23, -161.89) * mm});
            skLineSegment(sketch, "E282", {"start": v(-57.23, -161.89) * mm, "end": v(-54.61, -160.15) * mm});
            skLineSegment(sketch, "E283", {"start": v(-54.61, -160.15) * mm, "end": v(-53.54, -157.7) * mm});
            skLineSegment(sketch, "E284", {"start": v(-53.54, -157.7) * mm, "end": v(-52.54, -152.64) * mm});
            skLineSegment(sketch, "E285", {"start": v(-52.54, -152.64) * mm, "end": v(-51.74, -148.55) * mm});
            skLineSegment(sketch, "E286", {"start": v(-51.74, -148.55) * mm, "end": v(-52.54, -138.85) * mm});
            skLineSegment(sketch, "E287", {"start": v(-52.54, -138.85) * mm, "end": v(-52.96, -133.83) * mm});
            skLineSegment(sketch, "E288", {"start": v(-52.96, -133.83) * mm, "end": v(-54.3, -130.15) * mm});
            skLineSegment(sketch, "E289", {"start": v(-54.3, -130.15) * mm, "end": v(-58, -120.08) * mm});
            skLineSegment(sketch, "E290", {"start": v(-58, -120.08) * mm, "end": v(-59.14, -113.84) * mm});
            skLineSegment(sketch, "E291", {"start": v(-59.14, -113.84) * mm, "end": v(-62.37, -101.36) * mm});
            skLineSegment(sketch, "E292", {"start": v(-62.37, -101.36) * mm, "end": v(-67.08, -86.82) * mm});
            skLineSegment(sketch, "E293", {"start": v(-67.08, -86.82) * mm, "end": v(-70.65, -75.8) * mm});
            skLineSegment(sketch, "E294", {"start": v(-70.65, -75.8) * mm, "end": v(-72.2, -73.1) * mm});
            skLineSegment(sketch, "E295", {"start": v(-72.2, -73.1) * mm, "end": v(-78.73, -69.85) * mm});
            skLineSegment(sketch, "E296", {"start": v(-78.73, -69.85) * mm, "end": v(-86.85, -64.91) * mm});
            skLineSegment(sketch, "E297", {"start": v(-86.85, -64.91) * mm, "end": v(-92.77, -61.31) * mm});
            skLineSegment(sketch, "E298", {"start": v(-92.77, -61.31) * mm, "end": v(-93.1, -62.44) * mm});
            skLineSegment(sketch, "E299", {"start": v(-93.1, -62.44) * mm, "end": v(-94.39, -62.5) * mm});
            skLineSegment(sketch, "E300", {"start": v(-94.39, -62.5) * mm, "end": v(-98.45, -64.55) * mm});
            skLineSegment(sketch, "E301", {"start": v(-98.45, -64.55) * mm, "end": v(-101.2, -65.95) * mm});
            skLineSegment(sketch, "E302", {"start": v(-101.2, -65.95) * mm, "end": v(-103.82, -67.28) * mm});
            skLineSegment(sketch, "E303", {"start": v(-103.82, -67.28) * mm, "end": v(-108.52, -67.2) * mm});
            skLineSegment(sketch, "E304", {"start": v(-108.52, -67.2) * mm, "end": v(-113.7, -65.96) * mm});
            skLineSegment(sketch, "E305", {"start": v(-113.7, -65.96) * mm, "end": v(-120.68, -64.3) * mm});
            skLineSegment(sketch, "E306", {"start": v(-120.68, -64.3) * mm, "end": v(-140.13, -61.84) * mm});
            skLineSegment(sketch, "E307", {"start": v(-140.13, -61.84) * mm, "end": v(-147.8, -60.07) * mm});
            skLineSegment(sketch, "E308", {"start": v(-147.8, -60.07) * mm, "end": v(-153.26, -59.65) * mm});
            skLineSegment(sketch, "E309", {"start": v(-153.26, -59.65) * mm, "end": v(-158.03, -60.48) * mm});
            skLineSegment(sketch, "E310", {"start": v(-158.03, -60.48) * mm, "end": v(-161.62, -62.06) * mm});
            skLineSegment(sketch, "E311", {"start": v(-161.62, -62.06) * mm, "end": v(-171.92, -68.6) * mm});
            skLineSegment(sketch, "E312", {"start": v(-171.92, -68.6) * mm, "end": v(-178.57, -76.9) * mm});
            skLineSegment(sketch, "E313", {"start": v(-178.57, -76.9) * mm, "end": v(-183.4, -84.13) * mm});
            skLineSegment(sketch, "E314", {"start": v(-183.4, -84.13) * mm, "end": v(-185.1, -86.7) * mm});
            skLineSegment(sketch, "E315", {"start": v(-185.1, -86.7) * mm, "end": v(-187.4, -88.44) * mm});
            skLineSegment(sketch, "E316", {"start": v(-187.4, -88.44) * mm, "end": v(-191.41, -91.49) * mm});
            skLineSegment(sketch, "E317", {"start": v(-191.41, -91.49) * mm, "end": v(-189.7, -93.45) * mm});
            skLineSegment(sketch, "E318", {"start": v(-189.7, -93.45) * mm, "end": v(-188.9, -94.37) * mm});
            skLineSegment(sketch, "E319", {"start": v(-188.9, -94.37) * mm, "end": v(-189.35, -95.8) * mm});
            skLineSegment(sketch, "E320", {"start": v(-189.35, -95.8) * mm, "end": v(-189.83, -97.34) * mm});
            skLineSegment(sketch, "E321", {"start": v(-189.83, -97.34) * mm, "end": v(-190.63, -99.92) * mm});
            skLineSegment(sketch, "E322", {"start": v(-190.63, -99.92) * mm, "end": v(-192.59, -102.33) * mm});
            skLineSegment(sketch, "E323", {"start": v(-192.59, -102.33) * mm, "end": v(-194.23, -105.8) * mm});
            skLineSegment(sketch, "E324", {"start": v(-194.23, -105.8) * mm, "end": v(-195.65, -107.27) * mm});
            skLineSegment(sketch, "E325", {"start": v(-195.65, -107.27) * mm, "end": v(-205.6, -110.8) * mm});
            skLineSegment(sketch, "E326", {"start": v(-205.6, -110.8) * mm, "end": v(-208.37, -110.98) * mm});
            skLineSegment(sketch, "E327", {"start": v(-208.37, -110.98) * mm, "end": v(-211.78, -111.2) * mm});
            skLineSegment(sketch, "E328", {"start": v(-211.78, -111.2) * mm, "end": v(-214.2, -108.22) * mm});
            skLineSegment(sketch, "E329", {"start": v(-214.2, -108.22) * mm, "end": v(-214.31, -106.4) * mm});
            skLineSegment(sketch, "E330", {"start": v(-214.31, -106.4) * mm, "end": v(-211.2, -98.46) * mm});
            skLineSegment(sketch, "E331", {"start": v(-211.2, -98.46) * mm, "end": v(-208.8, -92.35) * mm});
            skLineSegment(sketch, "E332", {"start": v(-208.8, -92.35) * mm, "end": v(-206.43, -88.4) * mm});
            skLineSegment(sketch, "E333", {"start": v(-206.43, -88.4) * mm, "end": v(-203.08, -85.53) * mm});
            skLineSegment(sketch, "E334", {"start": v(-203.08, -85.53) * mm, "end": v(-200.72, -81.39) * mm});
            skLineSegment(sketch, "E335", {"start": v(-200.72, -81.39) * mm, "end": v(-199.3, -76.92) * mm});
            skLineSegment(sketch, "E336", {"start": v(-199.3, -76.92) * mm, "end": v(-198.5, -74.34) * mm});
            skLineSegment(sketch, "E337", {"start": v(-198.5, -74.34) * mm, "end": v(-193.37, -70.34) * mm});
            skLineSegment(sketch, "E338", {"start": v(-193.37, -70.34) * mm, "end": v(-184.89, -62.72) * mm});
            skLineSegment(sketch, "E339", {"start": v(-184.89, -62.72) * mm, "end": v(-178.3, -55.84) * mm});
            skLineSegment(sketch, "E340", {"start": v(-178.3, -55.84) * mm, "end": v(-174.29, -50.71) * mm});
            skLineSegment(sketch, "E341", {"start": v(-174.29, -50.71) * mm, "end": v(-170.23, -47.24) * mm});
            skLineSegment(sketch, "E342", {"start": v(-170.23, -47.24) * mm, "end": v(-166.64, -45.07) * mm});
            skLineSegment(sketch, "E343", {"start": v(-166.64, -45.07) * mm, "end": v(-162.23, -43.3) * mm});
            skLineSegment(sketch, "E344", {"start": v(-162.23, -43.3) * mm, "end": v(-156.52, -41.83) * mm});
            skLineSegment(sketch, "E345", {"start": v(-156.52, -41.83) * mm, "end": v(-148.35, -40.77) * mm});
            skLineSegment(sketch, "E346", {"start": v(-148.35, -40.77) * mm, "end": v(-142.57, -40.03) * mm});
            skLineSegment(sketch, "E347", {"start": v(-142.57, -40.03) * mm, "end": v(-134.68, -39.89) * mm});
            skLineSegment(sketch, "E348", {"start": v(-134.68, -39.89) * mm, "end": v(-129.33, -39) * mm});
            skLineSegment(sketch, "E349", {"start": v(-129.33, -39) * mm, "end": v(-127.68, -37.66) * mm});
            skLineSegment(sketch, "E350", {"start": v(-127.68, -37.66) * mm, "end": v(-127.5, -35.07) * mm});
            skLineSegment(sketch, "E351", {"start": v(-127.5, -35.07) * mm, "end": v(-129.8, -21.88) * mm});
            skLineSegment(sketch, "E352", {"start": v(-129.8, -21.88) * mm, "end": v(-128.92, -12.45) * mm});
            skLineSegment(sketch, "E353", {"start": v(-128.92, -12.45) * mm, "end": v(-126.98, -6.92) * mm});
            skLineSegment(sketch, "E354", {"start": v(-126.98, -6.92) * mm, "end": v(-124.52, 0.09) * mm});
            skLineSegment(sketch, "E355", {"start": v(-124.52, 0.09) * mm, "end": v(-124.2, 5.44) * mm});
            skLineSegment(sketch, "E356", {"start": v(-124.2, 5.44) * mm, "end": v(-125.03, 5.8) * mm});
            skLineSegment(sketch, "E357", {"start": v(-125.03, 5.8) * mm, "end": v(-129.62, 4.68) * mm});
            skLineSegment(sketch, "E358", {"start": v(-129.62, 4.68) * mm, "end": v(-134.2, 2.27) * mm});
            skLineSegment(sketch, "E359", {"start": v(-134.2, 2.27) * mm, "end": v(-137.37, 0.6) * mm});
            skLineSegment(sketch, "E360", {"start": v(-137.37, 0.6) * mm, "end": v(-139.8, 0.33) * mm});
            skLineSegment(sketch, "E361", {"start": v(-139.8, 0.33) * mm, "end": v(-142.14, 0.06) * mm});
            skLineSegment(sketch, "E362", {"start": v(-142.14, 0.06) * mm, "end": v(-142.5, -2.73) * mm});
            skLineSegment(sketch, "E363", {"start": v(-142.5, -2.73) * mm, "end": v(-141.97, -4.55) * mm});
            skLineSegment(sketch, "E364", {"start": v(-141.97, -4.55) * mm, "end": v(-142.27, -7.37) * mm});
            skLineSegment(sketch, "E365", {"start": v(-142.27, -7.37) * mm, "end": v(-143.62, -8.96) * mm});
            skLineSegment(sketch, "E366", {"start": v(-143.62, -8.96) * mm, "end": v(-145.33, -10.97) * mm});
            skLineSegment(sketch, "E367", {"start": v(-145.33, -10.97) * mm, "end": v(-148.03, -12.6) * mm});
            skLineSegment(sketch, "E368", {"start": v(-148.03, -12.6) * mm, "end": v(-150.92, -14.36) * mm});
            skLineSegment(sketch, "E369", {"start": v(-150.92, -14.36) * mm, "end": v(-156.75, -17.9) * mm});
            skLineSegment(sketch, "E370", {"start": v(-156.75, -17.9) * mm, "end": v(-161.91, -17.49) * mm});
            skLineSegment(sketch, "E371", {"start": v(-161.91, -17.49) * mm, "end": v(-165.32, -14.9) * mm});
            skLineSegment(sketch, "E372", {"start": v(-165.32, -14.9) * mm, "end": v(-169.22, -13) * mm});
            skLineSegment(sketch, "E373", {"start": v(-169.22, -13) * mm, "end": v(-170.75, -10.54) * mm});
            skLineSegment(sketch, "E374", {"start": v(-170.75, -10.54) * mm, "end": v(-172.48, -7.73) * mm});
            skLineSegment(sketch, "E375", {"start": v(-172.48, -7.73) * mm, "end": v(-173.28, -3.01) * mm});
            skLineSegment(sketch, "E376", {"start": v(-173.28, -3.01) * mm, "end": v(-173.57, 3.63) * mm});
            skLineSegment(sketch, "E377", {"start": v(-173.57, 3.63) * mm, "end": v(-173.88, 10.5) * mm});
            skLineSegment(sketch, "E378", {"start": v(-173.88, 10.5) * mm, "end": v(-174, 13.17) * mm});
            skLineSegment(sketch, "E379", {"start": v(-174, 13.17) * mm, "end": v(-176.81, 18.7) * mm});
            skLineSegment(sketch, "E380", {"start": v(-176.81, 18.7) * mm, "end": v(-175.87, 21.76) * mm});
            skLineSegment(sketch, "E381", {"start": v(-175.87, 21.76) * mm, "end": v(-174.34, 23.46) * mm});
            skLineSegment(sketch, "E382", {"start": v(-174.34, 23.46) * mm, "end": v(-174.99, 29.58) * mm});
            skLineSegment(sketch, "E383", {"start": v(-174.99, 29.58) * mm, "end": v(-176.76, 38.18) * mm});
            skLineSegment(sketch, "E384", {"start": v(-176.76, 38.18) * mm, "end": v(-178.52, 43) * mm});
            skLineSegment(sketch, "E385", {"start": v(-178.52, 43) * mm, "end": v(-178.7, 45.7) * mm});
            skLineSegment(sketch, "E386", {"start": v(-178.7, 45.7) * mm, "end": v(-180, 55.67) * mm});
            skLineSegment(sketch, "E387", {"start": v(-180, 55.67) * mm, "end": v(-180.39, 58.72) * mm});
            skLineSegment(sketch, "E388", {"start": v(-180.39, 58.72) * mm, "end": v(-179.7, 61.67) * mm});
            skLineSegment(sketch, "E389", {"start": v(-179.7, 61.67) * mm, "end": v(-180.52, 63.5) * mm});
            skLineSegment(sketch, "E390", {"start": v(-180.52, 63.5) * mm, "end": v(-180.82, 66.63) * mm});
            skLineSegment(sketch, "E391", {"start": v(-180.82, 66.63) * mm, "end": v(-188.3, 70.93) * mm});
            skLineSegment(sketch, "E392", {"start": v(-188.3, 70.93) * mm, "end": v(-193, 76.33) * mm});
            skLineSegment(sketch, "E393", {"start": v(-193, 76.33) * mm, "end": v(-196.59, 81.57) * mm});
            skLineSegment(sketch, "E394", {"start": v(-196.59, 81.57) * mm, "end": v(-180.47, 75.63) * mm});
            skLineSegment(sketch, "E395", {"start": v(-180.47, 75.63) * mm, "end": v(-182.82, 79.69) * mm});
            skLineSegment(sketch, "E396", {"start": v(-182.82, 79.69) * mm, "end": v(-176.82, 78.69) * mm});
            skLineSegment(sketch, "E397", {"start": v(-176.82, 78.69) * mm, "end": v(-174.41, 77.75) * mm});
            skLineSegment(sketch, "E398", {"start": v(-174.41, 77.75) * mm, "end": v(-173.18, 76.33) * mm});
            skLineSegment(sketch, "E399", {"start": v(-173.18, 76.33) * mm, "end": v(-171.3, 77.33) * mm});
            skLineSegment(sketch, "E400", {"start": v(-171.3, 77.33) * mm, "end": v(-166.18, 81.27) * mm});
            skLineSegment(sketch, "E401", {"start": v(-166.18, 81.27) * mm, "end": v(-164.16, 82.83) * mm});
            skLineSegment(sketch, "E402", {"start": v(-164.16, 82.83) * mm, "end": v(-157.53, 85.99) * mm});
            skLineSegment(sketch, "E403", {"start": v(-157.53, 85.99) * mm, "end": v(-153.47, 87.16) * mm});
            skLineSegment(sketch, "E404", {"start": v(-153.47, 87.16) * mm, "end": v(-149.73, 88.25) * mm});
            skLineSegment(sketch, "E405", {"start": v(-149.73, 88.25) * mm, "end": v(-147.24, 88.05) * mm});
            skLineSegment(sketch, "E406", {"start": v(-147.24, 88.05) * mm, "end": v(-146.03, 87.95) * mm});
            skLineSegment(sketch, "E407", {"start": v(-146.03, 87.95) * mm, "end": v(-142.93, 89.47) * mm});
            skLineSegment(sketch, "E408", {"start": v(-142.93, 89.47) * mm, "end": v(-139.52, 90.17) * mm});
            skLineSegment(sketch, "E409", {"start": v(-139.52, 90.17) * mm, "end": v(-136.87, 90.72) * mm});
            skLineSegment(sketch, "E410", {"start": v(-136.87, 90.72) * mm, "end": v(-132.81, 91.56) * mm});
            skLineSegment(sketch, "E411", {"start": v(-132.81, 91.56) * mm, "end": v(-128.56, 90.7) * mm});
            skLineSegment(sketch, "E412", {"start": v(-128.56, 90.7) * mm, "end": v(-126.1, 91.18) * mm});
            skLineSegment(sketch, "E413", {"start": v(-126.1, 91.18) * mm, "end": v(-118.92, 90.3) * mm});
            skLineSegment(sketch, "E414", {"start": v(-118.92, 90.3) * mm, "end": v(-116.62, 88.76) * mm});
            skLineSegment(sketch, "E415", {"start": v(-116.62, 88.76) * mm, "end": v(-114.1, 88.35) * mm});
            skLineSegment(sketch, "E416", {"start": v(-114.1, 88.35) * mm, "end": v(-109.98, 86.88) * mm});
            skLineSegment(sketch, "E417", {"start": v(-109.98, 86.88) * mm, "end": v(-103.73, 82.82) * mm});
            skLineSegment(sketch, "E418", {"start": v(-103.73, 82.82) * mm, "end": v(-101.25, 82.12) * mm});
            skLineSegment(sketch, "E419", {"start": v(-101.25, 82.12) * mm, "end": v(-97.67, 80.24) * mm});
            skLineSegment(sketch, "E420", {"start": v(-97.67, 80.24) * mm, "end": v(-96.84, 79) * mm});
            skLineSegment(sketch, "E421", {"start": v(-96.84, 79) * mm, "end": v(-92.9, 77.12) * mm});
            skLineSegment(sketch, "E422", {"start": v(-92.9, 77.12) * mm, "end": v(-91.07, 75.4) * mm});
            skLineSegment(sketch, "E423", {"start": v(-91.07, 75.4) * mm, "end": v(-90.62, 74.98) * mm});
            skLineSegment(sketch, "E424", {"start": v(-90.62, 74.98) * mm, "end": v(-87.19, 73.17) * mm});
            skLineSegment(sketch, "E425", {"start": v(-87.19, 73.17) * mm, "end": v(-85.6, 71.11) * mm});
            skLineSegment(sketch, "E426", {"start": v(-85.6, 71.11) * mm, "end": v(-83.24, 70.17) * mm});
            skLineSegment(sketch, "E427", {"start": v(-83.24, 70.17) * mm, "end": v(-81, 68.17) * mm});
            skLineSegment(sketch, "E428", {"start": v(-81, 68.17) * mm, "end": v(-79.59, 65.4) * mm});
            skLineSegment(sketch, "E429", {"start": v(-79.59, 65.4) * mm, "end": v(-77.83, 65.05) * mm});
            skLineSegment(sketch, "E430", {"start": v(-77.83, 65.05) * mm, "end": v(-75.12, 63.64) * mm});
            skLineSegment(sketch, "E431", {"start": v(-75.12, 63.64) * mm, "end": v(-73.41, 61.29) * mm});
            skLineSegment(sketch, "E432", {"start": v(-73.41, 61.29) * mm, "end": v(-72.88, 59.4) * mm});
            skLineSegment(sketch, "E433", {"start": v(-72.88, 59.4) * mm, "end": v(-70.52, 57.34) * mm});
            skLineSegment(sketch, "E434", {"start": v(-70.52, 57.34) * mm, "end": v(-68.34, 58.22) * mm});
            skLineSegment(sketch, "E435", {"start": v(-68.34, 58.22) * mm, "end": v(-65.7, 61.51) * mm});
            skLineSegment(sketch, "E436", {"start": v(-65.7, 61.51) * mm, "end": v(-62.91, 64.97) * mm});
            skLineSegment(sketch, "E437", {"start": v(-62.91, 64.97) * mm, "end": v(-59.4, 67.27) * mm});
            skLineSegment(sketch, "E438", {"start": v(-59.4, 67.27) * mm, "end": v(-54.2, 68.63) * mm});
            skLineSegment(sketch, "E439", {"start": v(-54.2, 68.63) * mm, "end": v(-50.44, 69.62) * mm});
            skLineSegment(sketch, "E440", {"start": v(-50.44, 69.62) * mm, "end": v(-40.07, 77.1) * mm});
            skLineSegment(sketch, "E441", {"start": v(-40.07, 77.1) * mm, "end": v(-31.3, 85.34) * mm});
            skLineSegment(sketch, "E442", {"start": v(-31.3, 85.34) * mm, "end": v(-27.8, 88.62) * mm});
            skLineSegment(sketch, "E443", {"start": v(-27.8, 88.62) * mm, "end": v(-23.11, 96.7) * mm});
            skLineSegment(sketch, "E444", {"start": v(-23.11, 96.7) * mm, "end": v(-19.84, 102.35) * mm});
            skLineSegment(sketch, "E445", {"start": v(-19.84, 102.35) * mm, "end": v(-18.1, 107.32) * mm});
            skLineSegment(sketch, "E446", {"start": v(-18.1, 107.32) * mm, "end": v(-16.43, 112.12) * mm});
            skLineSegment(sketch, "E447", {"start": v(-16.43, 112.12) * mm, "end": v(-14.34, 114.78) * mm});
            skLineSegment(sketch, "E448", {"start": v(-14.34, 114.78) * mm, "end": v(-12.38, 117.29) * mm});
            skLineSegment(sketch, "E449", {"start": v(-12.38, 117.29) * mm, "end": v(-10, 120.31) * mm});
            skLineSegment(sketch, "E450", {"start": v(-10, 120.31) * mm, "end": v(-8.52, 124.07) * mm});
            skLineSegment(sketch, "E451", {"start": v(-8.52, 124.07) * mm, "end": v(-7.35, 127.02) * mm});
            skLineSegment(sketch, "E452", {"start": v(-7.35, 127.02) * mm, "end": v(-5.69, 128.33) * mm});
            skLineSegment(sketch, "E453", {"start": v(-5.69, 128.33) * mm, "end": v(-4.75, 129.07) * mm});
            skLineSegment(sketch, "E454", {"start": v(-4.75, 129.07) * mm, "end": v(-6.57, 130.03) * mm});
            skLineSegment(sketch, "E455", {"start": v(-6.57, 130.03) * mm, "end": v(-9.33, 131.5) * mm});
            skLineSegment(sketch, "E456", {"start": v(-9.33, 131.5) * mm, "end": v(-11.45, 134.27) * mm});
            skLineSegment(sketch, "E457", {"start": v(-11.45, 134.27) * mm, "end": v(-12.22, 137.32) * mm});
            skLineSegment(sketch, "E458", {"start": v(-12.22, 137.32) * mm, "end": v(-12.7, 139.24) * mm});
            skLineSegment(sketch, "E459", {"start": v(-12.7, 139.24) * mm, "end": v(-12.91, 140.1) * mm});
            skLineSegment(sketch, "E460", {"start": v(-12.91, 140.1) * mm, "end": v(-14.1, 140.93) * mm});
            skLineSegment(sketch, "E461", {"start": v(-14.1, 140.93) * mm, "end": v(-13.75, 142.16) * mm});
            skLineSegment(sketch, "E462", {"start": v(-13.75, 142.16) * mm, "end": v(-12.52, 143.99) * mm});
            skLineSegment(sketch, "E463", {"start": v(-12.52, 143.99) * mm, "end": v(-12.58, 145.75) * mm});
            skLineSegment(sketch, "E464", {"start": v(-12.58, 145.75) * mm, "end": v(-12.62, 147.15) * mm});
            skLineSegment(sketch, "E465", {"start": v(-12.62, 147.15) * mm, "end": v(-12.65, 147.86) * mm});
            skLineSegment(sketch, "E466", {"start": v(-12.65, 147.86) * mm, "end": v(-18.05, 148.4) * mm});
            skLineSegment(sketch, "E467", {"start": v(-18.05, 148.4) * mm, "end": v(-20.75, 149.63) * mm});
            skLineSegment(sketch, "E468", {"start": v(-20.75, 149.63) * mm, "end": v(-17.52, 152.63) * mm});
            skLineSegment(sketch, "E469", {"start": v(-17.52, 152.63) * mm, "end": v(-15.37, 154) * mm});
            skLineSegment(sketch, "E470", {"start": v(-25.48, 59.34) * mm, "end": v(-25.96, 52.06) * mm});
            skLineSegment(sketch, "E471", {"start": v(-25.96, 52.06) * mm, "end": v(-33.19, 46.75) * mm});
            skLineSegment(sketch, "E472", {"start": v(-33.19, 46.75) * mm, "end": v(-32.91, 46.96) * mm});
            skLineSegment(sketch, "E473", {"start": v(-32.91, 46.96) * mm, "end": v(-35.1, 49.09) * mm});
            skLineSegment(sketch, "E474", {"start": v(-35.1, 49.09) * mm, "end": v(-40.63, 48.93) * mm});
            skLineSegment(sketch, "E475", {"start": v(-40.63, 48.93) * mm, "end": v(-43.56, 47.34) * mm});
            skLineSegment(sketch, "E476", {"start": v(-43.56, 47.34) * mm, "end": v(-49.03, 49.09) * mm});
            skLineSegment(sketch, "E477", {"start": v(-49.03, 49.09) * mm, "end": v(-51.1, 47.44) * mm});
            skLineSegment(sketch, "E478", {"start": v(-51.1, 47.44) * mm, "end": v(-52.6, 47.6) * mm});
            skLineSegment(sketch, "E479", {"start": v(-52.6, 47.6) * mm, "end": v(-48.45, 51.37) * mm});
            skLineSegment(sketch, "E480", {"start": v(-48.45, 51.37) * mm, "end": v(-45.68, 51.53) * mm});
            skLineSegment(sketch, "E481", {"start": v(-45.68, 51.53) * mm, "end": v(-40.1, 55.04) * mm});
            skLineSegment(sketch, "E482", {"start": v(-40.1, 55.04) * mm, "end": v(-37.12, 52.49) * mm});
            skLineSegment(sketch, "E483", {"start": v(-37.12, 52.49) * mm, "end": v(-25.48, 59.34) * mm});
            skLineSegment(sketch, "E484", {"start": v(-134.3, 16.79) * mm, "end": v(-134.58, 18.5) * mm});
            skLineSegment(sketch, "E485", {"start": v(-134.58, 18.5) * mm, "end": v(-135.73, 18.72) * mm});
            skLineSegment(sketch, "E486", {"start": v(-135.73, 18.72) * mm, "end": v(-136.16, 20.8) * mm});
            skLineSegment(sketch, "E487", {"start": v(-136.16, 20.8) * mm, "end": v(-133.58, 26.04) * mm});
            skLineSegment(sketch, "E488", {"start": v(-133.58, 26.04) * mm, "end": v(-131.71, 27.98) * mm});
            skLineSegment(sketch, "E489", {"start": v(-131.71, 27.98) * mm, "end": v(-130.28, 32.29) * mm});
            skLineSegment(sketch, "E490", {"start": v(-130.28, 32.29) * mm, "end": v(-126.61, 27.4) * mm});
            skLineSegment(sketch, "E491", {"start": v(-126.61, 27.4) * mm, "end": v(-124.79, 24.97) * mm});
            skLineSegment(sketch, "E492", {"start": v(-124.79, 24.97) * mm, "end": v(-124.32, 21.67) * mm});
            skLineSegment(sketch, "E493", {"start": v(-124.32, 21.67) * mm, "end": v(-134.3, 16.79) * mm});
            skLineSegment(sketch, "E494", {"start": v(-139.18, 8.17) * mm, "end": v(-138.75, 5.66) * mm});
            skLineSegment(sketch, "E495", {"start": v(-138.75, 5.66) * mm, "end": v(-136.24, 5.88) * mm});
            skLineSegment(sketch, "E496", {"start": v(-136.24, 5.88) * mm, "end": v(-134.51, 5.23) * mm});
            skLineSegment(sketch, "E497", {"start": v(-134.51, 5.23) * mm, "end": v(-132, 6.74) * mm});
            skLineSegment(sketch, "E498", {"start": v(-132, 6.74) * mm, "end": v(-123.02, 10.4) * mm});
            skLineSegment(sketch, "E499", {"start": v(-123.02, 10.4) * mm, "end": v(-122.8, 15.92) * mm});
            skLineSegment(sketch, "E500", {"start": v(-122.8, 15.92) * mm, "end": v(-123.53, 18.15) * mm});
            skLineSegment(sketch, "E501", {"start": v(-123.53, 18.15) * mm, "end": v(-133, 13.41) * mm});
            skLineSegment(sketch, "E502", {"start": v(-133, 13.41) * mm, "end": v(-135.95, 10.04) * mm});
            skLineSegment(sketch, "E503", {"start": v(-135.95, 10.04) * mm, "end": v(-139.18, 8.17) * mm});
            skSolve(sketch);
        }
        {
            var Q0;
            Q0=makeQuery(id+"F0.imprint","IMPRINT",FACE,{"disambiguationData":[TD([[makeQuery(id+"F0.imprint","IMPRINT",EDGE,{"derivedFrom":sQuery(id+"F0.wireOp",EDGE,"E0")}),-1.0]])]});
            extrude(context, id + "F1", {"entities" : qUnion([Q0]), "depth" : 6.35 * mm, "offsetDistance" : 25.4 * mm});
        }
        {
            var Q0;
            Q0=makeQuery(id+"F1.opExtrude","SWEPT_BODY",BODY,{"disambiguationData":[OSD([sQuery(id+"F0.wireOp",EDGE,"E0"),sQuery(id+"F0.wireOp",EDGE,"E1"),sQuery(id+"F0.wireOp",EDGE,"E2"),sQuery(id+"F0.wireOp",EDGE,"E3"),sQuery(id+"F0.wireOp",EDGE,"E4"),sQuery(id+"F0.wireOp",EDGE,"E5"),sQuery(id+"F0.wireOp",EDGE,"E6"),sQuery(id+"F0.wireOp",EDGE,"E7"),sQuery(id+"F0.wireOp",EDGE,"E8"),sQuery(id+"F0.wireOp",EDGE,"E9"),sQuery(id+"F0.wireOp",EDGE,"E10"),sQuery(id+"F0.wireOp",EDGE,"E11"),sQuery(id+"F0.wireOp",EDGE,"E12"),sQuery(id+"F0.wireOp",EDGE,"E13"),sQuery(id+"F0.wireOp",EDGE,"E14"),sQuery(id+"F0.wireOp",EDGE,"E15"),sQuery(id+"F0.wireOp",EDGE,"E16"),sQuery(id+"F0.wireOp",EDGE,"E17"),sQuery(id+"F0.wireOp",EDGE,"E18"),sQuery(id+"F0.wireOp",EDGE,"E19"),sQuery(id+"F0.wireOp",EDGE,"E20"),sQuery(id+"F0.wireOp",EDGE,"E21"),sQuery(id+"F0.wireOp",EDGE,"E22"),sQuery(id+"F0.wireOp",EDGE,"E23"),sQuery(id+"F0.wireOp",EDGE,"E24"),sQuery(id+"F0.wireOp",EDGE,"E25"),sQuery(id+"F0.wireOp",EDGE,"E26"),sQuery(id+"F0.wireOp",EDGE,"E27"),sQuery(id+"F0.wireOp",EDGE,"E28"),sQuery(id+"F0.wireOp",EDGE,"E29"),sQuery(id+"F0.wireOp",EDGE,"E30"),sQuery(id+"F0.wireOp",EDGE,"E31"),sQuery(id+"F0.wireOp",EDGE,"E32"),sQuery(id+"F0.wireOp",EDGE,"E33"),sQuery(id+"F0.wireOp",EDGE,"E34"),sQuery(id+"F0.wireOp",EDGE,"E35"),sQuery(id+"F0.wireOp",EDGE,"E36"),sQuery(id+"F0.wireOp",EDGE,"E37"),sQuery(id+"F0.wireOp",EDGE,"E38"),sQuery(id+"F0.wireOp",EDGE,"E39"),sQuery(id+"F0.wireOp",EDGE,"E40"),sQuery(id+"F0.wireOp",EDGE,"E41"),sQuery(id+"F0.wireOp",EDGE,"E42"),sQuery(id+"F0.wireOp",EDGE,"E43"),sQuery(id+"F0.wireOp",EDGE,"E44"),sQuery(id+"F0.wireOp",EDGE,"E45"),sQuery(id+"F0.wireOp",EDGE,"E46"),sQuery(id+"F0.wireOp",EDGE,"E47"),sQuery(id+"F0.wireOp",EDGE,"E48"),sQuery(id+"F0.wireOp",EDGE,"E49"),sQuery(id+"F0.wireOp",EDGE,"E50"),sQuery(id+"F0.wireOp",EDGE,"E51"),sQuery(id+"F0.wireOp",EDGE,"E52"),sQuery(id+"F0.wireOp",EDGE,"E53"),sQuery(id+"F0.wireOp",EDGE,"E54"),sQuery(id+"F0.wireOp",EDGE,"E55"),sQuery(id+"F0.wireOp",EDGE,"E56"),sQuery(id+"F0.wireOp",EDGE,"E57"),sQuery(id+"F0.wireOp",EDGE,"E58"),sQuery(id+"F0.wireOp",EDGE,"E59"),sQuery(id+"F0.wireOp",EDGE,"E60"),sQuery(id+"F0.wireOp",EDGE,"E61"),sQuery(id+"F0.wireOp",EDGE,"E62"),sQuery(id+"F0.wireOp",EDGE,"E63"),sQuery(id+"F0.wireOp",EDGE,"E64"),sQuery(id+"F0.wireOp",EDGE,"E65"),sQuery(id+"F0.wireOp",EDGE,"E66"),sQuery(id+"F0.wireOp",EDGE,"E67"),sQuery(id+"F0.wireOp",EDGE,"E68"),sQuery(id+"F0.wireOp",EDGE,"E69"),sQuery(id+"F0.wireOp",EDGE,"E70"),sQuery(id+"F0.wireOp",EDGE,"E71"),sQuery(id+"F0.wireOp",EDGE,"E72"),sQuery(id+"F0.wireOp",EDGE,"E73"),sQuery(id+"F0.wireOp",EDGE,"E74"),sQuery(id+"F0.wireOp",EDGE,"E75"),sQuery(id+"F0.wireOp",EDGE,"E76"),sQuery(id+"F0.wireOp",EDGE,"E77"),sQuery(id+"F0.wireOp",EDGE,"E78"),sQuery(id+"F0.wireOp",EDGE,"E79"),sQuery(id+"F0.wireOp",EDGE,"E80"),sQuery(id+"F0.wireOp",EDGE,"E81"),sQuery(id+"F0.wireOp",EDGE,"E82"),sQuery(id+"F0.wireOp",EDGE,"E83"),sQuery(id+"F0.wireOp",EDGE,"E84"),sQuery(id+"F0.wireOp",EDGE,"E85"),sQuery(id+"F0.wireOp",EDGE,"E86"),sQuery(id+"F0.wireOp",EDGE,"E87"),sQuery(id+"F0.wireOp",EDGE,"E88"),sQuery(id+"F0.wireOp",EDGE,"E89"),sQuery(id+"F0.wireOp",EDGE,"E90"),sQuery(id+"F0.wireOp",EDGE,"E91"),sQuery(id+"F0.wireOp",EDGE,"E92"),sQuery(id+"F0.wireOp",EDGE,"E93"),sQuery(id+"F0.wireOp",EDGE,"E94"),sQuery(id+"F0.wireOp",EDGE,"E95"),sQuery(id+"F0.wireOp",EDGE,"E96"),sQuery(id+"F0.wireOp",EDGE,"E97"),sQuery(id+"F0.wireOp",EDGE,"E98"),sQuery(id+"F0.wireOp",EDGE,"E99"),sQuery(id+"F0.wireOp",EDGE,"E100"),sQuery(id+"F0.wireOp",EDGE,"E101"),sQuery(id+"F0.wireOp",EDGE,"E102"),sQuery(id+"F0.wireOp",EDGE,"E103"),sQuery(id+"F0.wireOp",EDGE,"E104"),sQuery(id+"F0.wireOp",EDGE,"E105"),sQuery(id+"F0.wireOp",EDGE,"E106"),sQuery(id+"F0.wireOp",EDGE,"E107"),sQuery(id+"F0.wireOp",EDGE,"E108"),sQuery(id+"F0.wireOp",EDGE,"E109"),sQuery(id+"F0.wireOp",EDGE,"E110"),sQuery(id+"F0.wireOp",EDGE,"E111"),sQuery(id+"F0.wireOp",EDGE,"E112"),sQuery(id+"F0.wireOp",EDGE,"E113"),sQuery(id+"F0.wireOp",EDGE,"E114"),sQuery(id+"F0.wireOp",EDGE,"E115"),sQuery(id+"F0.wireOp",EDGE,"E116"),sQuery(id+"F0.wireOp",EDGE,"E117"),sQuery(id+"F0.wireOp",EDGE,"E118"),sQuery(id+"F0.wireOp",EDGE,"E119"),sQuery(id+"F0.wireOp",EDGE,"E120"),sQuery(id+"F0.wireOp",EDGE,"E121"),sQuery(id+"F0.wireOp",EDGE,"E122"),sQuery(id+"F0.wireOp",EDGE,"E123"),sQuery(id+"F0.wireOp",EDGE,"E124"),sQuery(id+"F0.wireOp",EDGE,"E125"),sQuery(id+"F0.wireOp",EDGE,"E126"),sQuery(id+"F0.wireOp",EDGE,"E127"),sQuery(id+"F0.wireOp",EDGE,"E128"),sQuery(id+"F0.wireOp",EDGE,"E129"),sQuery(id+"F0.wireOp",EDGE,"E130"),sQuery(id+"F0.wireOp",EDGE,"E131"),sQuery(id+"F0.wireOp",EDGE,"E132"),sQuery(id+"F0.wireOp",EDGE,"E133"),sQuery(id+"F0.wireOp",EDGE,"E134"),sQuery(id+"F0.wireOp",EDGE,"E135"),sQuery(id+"F0.wireOp",EDGE,"E136"),sQuery(id+"F0.wireOp",EDGE,"E137"),sQuery(id+"F0.wireOp",EDGE,"E138"),sQuery(id+"F0.wireOp",EDGE,"E139"),sQuery(id+"F0.wireOp",EDGE,"E140"),sQuery(id+"F0.wireOp",EDGE,"E141"),sQuery(id+"F0.wireOp",EDGE,"E142"),sQuery(id+"F0.wireOp",EDGE,"E143"),sQuery(id+"F0.wireOp",EDGE,"E144"),sQuery(id+"F0.wireOp",EDGE,"E145"),sQuery(id+"F0.wireOp",EDGE,"E146"),sQuery(id+"F0.wireOp",EDGE,"E147"),sQuery(id+"F0.wireOp",EDGE,"E148"),sQuery(id+"F0.wireOp",EDGE,"E149"),sQuery(id+"F0.wireOp",EDGE,"E150"),sQuery(id+"F0.wireOp",EDGE,"E151"),sQuery(id+"F0.wireOp",EDGE,"E152"),sQuery(id+"F0.wireOp",EDGE,"E153"),sQuery(id+"F0.wireOp",EDGE,"E154"),sQuery(id+"F0.wireOp",EDGE,"E155"),sQuery(id+"F0.wireOp",EDGE,"E156"),sQuery(id+"F0.wireOp",EDGE,"E157"),sQuery(id+"F0.wireOp",EDGE,"E158"),sQuery(id+"F0.wireOp",EDGE,"E159"),sQuery(id+"F0.wireOp",EDGE,"E160"),sQuery(id+"F0.wireOp",EDGE,"E161"),sQuery(id+"F0.wireOp",EDGE,"E162"),sQuery(id+"F0.wireOp",EDGE,"E163"),sQuery(id+"F0.wireOp",EDGE,"E164"),sQuery(id+"F0.wireOp",EDGE,"E165"),sQuery(id+"F0.wireOp",EDGE,"E166"),sQuery(id+"F0.wireOp",EDGE,"E167"),sQuery(id+"F0.wireOp",EDGE,"E168"),sQuery(id+"F0.wireOp",EDGE,"E169"),sQuery(id+"F0.wireOp",EDGE,"E170"),sQuery(id+"F0.wireOp",EDGE,"E171"),sQuery(id+"F0.wireOp",EDGE,"E172"),sQuery(id+"F0.wireOp",EDGE,"E173"),sQuery(id+"F0.wireOp",EDGE,"E174"),sQuery(id+"F0.wireOp",EDGE,"E175"),sQuery(id+"F0.wireOp",EDGE,"E176"),sQuery(id+"F0.wireOp",EDGE,"E177"),sQuery(id+"F0.wireOp",EDGE,"E178"),sQuery(id+"F0.wireOp",EDGE,"E179"),sQuery(id+"F0.wireOp",EDGE,"E180"),sQuery(id+"F0.wireOp",EDGE,"E181"),sQuery(id+"F0.wireOp",EDGE,"E182"),sQuery(id+"F0.wireOp",EDGE,"E183"),sQuery(id+"F0.wireOp",EDGE,"E184"),sQuery(id+"F0.wireOp",EDGE,"E185"),sQuery(id+"F0.wireOp",EDGE,"E186"),sQuery(id+"F0.wireOp",EDGE,"E187"),sQuery(id+"F0.wireOp",EDGE,"E188"),sQuery(id+"F0.wireOp",EDGE,"E189"),sQuery(id+"F0.wireOp",EDGE,"E190"),sQuery(id+"F0.wireOp",EDGE,"E191"),sQuery(id+"F0.wireOp",EDGE,"E192"),sQuery(id+"F0.wireOp",EDGE,"E193"),sQuery(id+"F0.wireOp",EDGE,"E194"),sQuery(id+"F0.wireOp",EDGE,"E195"),sQuery(id+"F0.wireOp",EDGE,"E196"),sQuery(id+"F0.wireOp",EDGE,"E197"),sQuery(id+"F0.wireOp",EDGE,"E198"),sQuery(id+"F0.wireOp",EDGE,"E199"),sQuery(id+"F0.wireOp",EDGE,"E200"),sQuery(id+"F0.wireOp",EDGE,"E201"),sQuery(id+"F0.wireOp",EDGE,"E202"),sQuery(id+"F0.wireOp",EDGE,"E203"),sQuery(id+"F0.wireOp",EDGE,"E204"),sQuery(id+"F0.wireOp",EDGE,"E205"),sQuery(id+"F0.wireOp",EDGE,"E206"),sQuery(id+"F0.wireOp",EDGE,"E207"),sQuery(id+"F0.wireOp",EDGE,"E208"),sQuery(id+"F0.wireOp",EDGE,"E209"),sQuery(id+"F0.wireOp",EDGE,"E210"),sQuery(id+"F0.wireOp",EDGE,"E211"),sQuery(id+"F0.wireOp",EDGE,"E212"),sQuery(id+"F0.wireOp",EDGE,"E213"),sQuery(id+"F0.wireOp",EDGE,"E214"),sQuery(id+"F0.wireOp",EDGE,"E215"),sQuery(id+"F0.wireOp",EDGE,"E216"),sQuery(id+"F0.wireOp",EDGE,"E217"),sQuery(id+"F0.wireOp",EDGE,"E218"),sQuery(id+"F0.wireOp",EDGE,"E219"),sQuery(id+"F0.wireOp",EDGE,"E220"),sQuery(id+"F0.wireOp",EDGE,"E221"),sQuery(id+"F0.wireOp",EDGE,"E222"),sQuery(id+"F0.wireOp",EDGE,"E223"),sQuery(id+"F0.wireOp",EDGE,"E224"),sQuery(id+"F0.wireOp",EDGE,"E225"),sQuery(id+"F0.wireOp",EDGE,"E226"),sQuery(id+"F0.wireOp",EDGE,"E227"),sQuery(id+"F0.wireOp",EDGE,"E228"),sQuery(id+"F0.wireOp",EDGE,"E229"),sQuery(id+"F0.wireOp",EDGE,"E230"),sQuery(id+"F0.wireOp",EDGE,"E231"),sQuery(id+"F0.wireOp",EDGE,"E232"),sQuery(id+"F0.wireOp",EDGE,"E233"),sQuery(id+"F0.wireOp",EDGE,"E234"),sQuery(id+"F0.wireOp",EDGE,"E235"),sQuery(id+"F0.wireOp",EDGE,"E236"),sQuery(id+"F0.wireOp",EDGE,"E237"),sQuery(id+"F0.wireOp",EDGE,"E238"),sQuery(id+"F0.wireOp",EDGE,"E239"),sQuery(id+"F0.wireOp",EDGE,"E240"),sQuery(id+"F0.wireOp",EDGE,"E241"),sQuery(id+"F0.wireOp",EDGE,"E242"),sQuery(id+"F0.wireOp",EDGE,"E243"),sQuery(id+"F0.wireOp",EDGE,"E244"),sQuery(id+"F0.wireOp",EDGE,"E245"),sQuery(id+"F0.wireOp",EDGE,"E246"),sQuery(id+"F0.wireOp",EDGE,"E247"),sQuery(id+"F0.wireOp",EDGE,"E248"),sQuery(id+"F0.wireOp",EDGE,"E249"),sQuery(id+"F0.wireOp",EDGE,"E250"),sQuery(id+"F0.wireOp",EDGE,"E251"),sQuery(id+"F0.wireOp",EDGE,"E252"),sQuery(id+"F0.wireOp",EDGE,"E253"),sQuery(id+"F0.wireOp",EDGE,"E254"),sQuery(id+"F0.wireOp",EDGE,"E255"),sQuery(id+"F0.wireOp",EDGE,"E256"),sQuery(id+"F0.wireOp",EDGE,"E257"),sQuery(id+"F0.wireOp",EDGE,"E258"),sQuery(id+"F0.wireOp",EDGE,"E259"),sQuery(id+"F0.wireOp",EDGE,"E260"),sQuery(id+"F0.wireOp",EDGE,"E261"),sQuery(id+"F0.wireOp",EDGE,"E262"),sQuery(id+"F0.wireOp",EDGE,"E263"),sQuery(id+"F0.wireOp",EDGE,"E264"),sQuery(id+"F0.wireOp",EDGE,"E265"),sQuery(id+"F0.wireOp",EDGE,"E266"),sQuery(id+"F0.wireOp",EDGE,"E267"),sQuery(id+"F0.wireOp",EDGE,"E268"),sQuery(id+"F0.wireOp",EDGE,"E269"),sQuery(id+"F0.wireOp",EDGE,"E270"),sQuery(id+"F0.wireOp",EDGE,"E271"),sQuery(id+"F0.wireOp",EDGE,"E272"),sQuery(id+"F0.wireOp",EDGE,"E273"),sQuery(id+"F0.wireOp",EDGE,"E274"),sQuery(id+"F0.wireOp",EDGE,"E275"),sQuery(id+"F0.wireOp",EDGE,"E276"),sQuery(id+"F0.wireOp",EDGE,"E277"),sQuery(id+"F0.wireOp",EDGE,"E278"),sQuery(id+"F0.wireOp",EDGE,"E279"),sQuery(id+"F0.wireOp",EDGE,"E280"),sQuery(id+"F0.wireOp",EDGE,"E281"),sQuery(id+"F0.wireOp",EDGE,"E282"),sQuery(id+"F0.wireOp",EDGE,"E283"),sQuery(id+"F0.wireOp",EDGE,"E284"),sQuery(id+"F0.wireOp",EDGE,"E285"),sQuery(id+"F0.wireOp",EDGE,"E286"),sQuery(id+"F0.wireOp",EDGE,"E287"),sQuery(id+"F0.wireOp",EDGE,"E288"),sQuery(id+"F0.wireOp",EDGE,"E289"),sQuery(id+"F0.wireOp",EDGE,"E290"),sQuery(id+"F0.wireOp",EDGE,"E291"),sQuery(id+"F0.wireOp",EDGE,"E292"),sQuery(id+"F0.wireOp",EDGE,"E293"),sQuery(id+"F0.wireOp",EDGE,"E294"),sQuery(id+"F0.wireOp",EDGE,"E295"),sQuery(id+"F0.wireOp",EDGE,"E296"),sQuery(id+"F0.wireOp",EDGE,"E297"),sQuery(id+"F0.wireOp",EDGE,"E298"),sQuery(id+"F0.wireOp",EDGE,"E299"),sQuery(id+"F0.wireOp",EDGE,"E300"),sQuery(id+"F0.wireOp",EDGE,"E301"),sQuery(id+"F0.wireOp",EDGE,"E302"),sQuery(id+"F0.wireOp",EDGE,"E303"),sQuery(id+"F0.wireOp",EDGE,"E304"),sQuery(id+"F0.wireOp",EDGE,"E305"),sQuery(id+"F0.wireOp",EDGE,"E306"),sQuery(id+"F0.wireOp",EDGE,"E307"),sQuery(id+"F0.wireOp",EDGE,"E308"),sQuery(id+"F0.wireOp",EDGE,"E309"),sQuery(id+"F0.wireOp",EDGE,"E310"),sQuery(id+"F0.wireOp",EDGE,"E311"),sQuery(id+"F0.wireOp",EDGE,"E312"),sQuery(id+"F0.wireOp",EDGE,"E313"),sQuery(id+"F0.wireOp",EDGE,"E314"),sQuery(id+"F0.wireOp",EDGE,"E315"),sQuery(id+"F0.wireOp",EDGE,"E316"),sQuery(id+"F0.wireOp",EDGE,"E317"),sQuery(id+"F0.wireOp",EDGE,"E318"),sQuery(id+"F0.wireOp",EDGE,"E319"),sQuery(id+"F0.wireOp",EDGE,"E320"),sQuery(id+"F0.wireOp",EDGE,"E321"),sQuery(id+"F0.wireOp",EDGE,"E322"),sQuery(id+"F0.wireOp",EDGE,"E323"),sQuery(id+"F0.wireOp",EDGE,"E324"),sQuery(id+"F0.wireOp",EDGE,"E325"),sQuery(id+"F0.wireOp",EDGE,"E326"),sQuery(id+"F0.wireOp",EDGE,"E327"),sQuery(id+"F0.wireOp",EDGE,"E328"),sQuery(id+"F0.wireOp",EDGE,"E329"),sQuery(id+"F0.wireOp",EDGE,"E330"),sQuery(id+"F0.wireOp",EDGE,"E331"),sQuery(id+"F0.wireOp",EDGE,"E332"),sQuery(id+"F0.wireOp",EDGE,"E333"),sQuery(id+"F0.wireOp",EDGE,"E334"),sQuery(id+"F0.wireOp",EDGE,"E335"),sQuery(id+"F0.wireOp",EDGE,"E336"),sQuery(id+"F0.wireOp",EDGE,"E337"),sQuery(id+"F0.wireOp",EDGE,"E338"),sQuery(id+"F0.wireOp",EDGE,"E339"),sQuery(id+"F0.wireOp",EDGE,"E340"),sQuery(id+"F0.wireOp",EDGE,"E341"),sQuery(id+"F0.wireOp",EDGE,"E342"),sQuery(id+"F0.wireOp",EDGE,"E343"),sQuery(id+"F0.wireOp",EDGE,"E344"),sQuery(id+"F0.wireOp",EDGE,"E345"),sQuery(id+"F0.wireOp",EDGE,"E346"),sQuery(id+"F0.wireOp",EDGE,"E347"),sQuery(id+"F0.wireOp",EDGE,"E348"),sQuery(id+"F0.wireOp",EDGE,"E349"),sQuery(id+"F0.wireOp",EDGE,"E350"),sQuery(id+"F0.wireOp",EDGE,"E351"),sQuery(id+"F0.wireOp",EDGE,"E352"),sQuery(id+"F0.wireOp",EDGE,"E353"),sQuery(id+"F0.wireOp",EDGE,"E354"),sQuery(id+"F0.wireOp",EDGE,"E355"),sQuery(id+"F0.wireOp",EDGE,"E356"),sQuery(id+"F0.wireOp",EDGE,"E357"),sQuery(id+"F0.wireOp",EDGE,"E358"),sQuery(id+"F0.wireOp",EDGE,"E359"),sQuery(id+"F0.wireOp",EDGE,"E360"),sQuery(id+"F0.wireOp",EDGE,"E361"),sQuery(id+"F0.wireOp",EDGE,"E362"),sQuery(id+"F0.wireOp",EDGE,"E363"),sQuery(id+"F0.wireOp",EDGE,"E364"),sQuery(id+"F0.wireOp",EDGE,"E365"),sQuery(id+"F0.wireOp",EDGE,"E366"),sQuery(id+"F0.wireOp",EDGE,"E367"),sQuery(id+"F0.wireOp",EDGE,"E368"),sQuery(id+"F0.wireOp",EDGE,"E369"),sQuery(id+"F0.wireOp",EDGE,"E370"),sQuery(id+"F0.wireOp",EDGE,"E371"),sQuery(id+"F0.wireOp",EDGE,"E372"),sQuery(id+"F0.wireOp",EDGE,"E373"),sQuery(id+"F0.wireOp",EDGE,"E374"),sQuery(id+"F0.wireOp",EDGE,"E375"),sQuery(id+"F0.wireOp",EDGE,"E376"),sQuery(id+"F0.wireOp",EDGE,"E377"),sQuery(id+"F0.wireOp",EDGE,"E378"),sQuery(id+"F0.wireOp",EDGE,"E379"),sQuery(id+"F0.wireOp",EDGE,"E380"),sQuery(id+"F0.wireOp",EDGE,"E381"),sQuery(id+"F0.wireOp",EDGE,"E382"),sQuery(id+"F0.wireOp",EDGE,"E383"),sQuery(id+"F0.wireOp",EDGE,"E384"),sQuery(id+"F0.wireOp",EDGE,"E385"),sQuery(id+"F0.wireOp",EDGE,"E386"),sQuery(id+"F0.wireOp",EDGE,"E387"),sQuery(id+"F0.wireOp",EDGE,"E388"),sQuery(id+"F0.wireOp",EDGE,"E389"),sQuery(id+"F0.wireOp",EDGE,"E390"),sQuery(id+"F0.wireOp",EDGE,"E391"),sQuery(id+"F0.wireOp",EDGE,"E392"),sQuery(id+"F0.wireOp",EDGE,"E393"),sQuery(id+"F0.wireOp",EDGE,"E394"),sQuery(id+"F0.wireOp",EDGE,"E395"),sQuery(id+"F0.wireOp",EDGE,"E396"),sQuery(id+"F0.wireOp",EDGE,"E397"),sQuery(id+"F0.wireOp",EDGE,"E398"),sQuery(id+"F0.wireOp",EDGE,"E399"),sQuery(id+"F0.wireOp",EDGE,"E400"),sQuery(id+"F0.wireOp",EDGE,"E401"),sQuery(id+"F0.wireOp",EDGE,"E402"),sQuery(id+"F0.wireOp",EDGE,"E403"),sQuery(id+"F0.wireOp",EDGE,"E404"),sQuery(id+"F0.wireOp",EDGE,"E405"),sQuery(id+"F0.wireOp",EDGE,"E406"),sQuery(id+"F0.wireOp",EDGE,"E407"),sQuery(id+"F0.wireOp",EDGE,"E408"),sQuery(id+"F0.wireOp",EDGE,"E409"),sQuery(id+"F0.wireOp",EDGE,"E410"),sQuery(id+"F0.wireOp",EDGE,"E411"),sQuery(id+"F0.wireOp",EDGE,"E412"),sQuery(id+"F0.wireOp",EDGE,"E413"),sQuery(id+"F0.wireOp",EDGE,"E414"),sQuery(id+"F0.wireOp",EDGE,"E415"),sQuery(id+"F0.wireOp",EDGE,"E416"),sQuery(id+"F0.wireOp",EDGE,"E417"),sQuery(id+"F0.wireOp",EDGE,"E418"),sQuery(id+"F0.wireOp",EDGE,"E419"),sQuery(id+"F0.wireOp",EDGE,"E420"),sQuery(id+"F0.wireOp",EDGE,"E421"),sQuery(id+"F0.wireOp",EDGE,"E422"),sQuery(id+"F0.wireOp",EDGE,"E423"),sQuery(id+"F0.wireOp",EDGE,"E424"),sQuery(id+"F0.wireOp",EDGE,"E425"),sQuery(id+"F0.wireOp",EDGE,"E426"),sQuery(id+"F0.wireOp",EDGE,"E427"),sQuery(id+"F0.wireOp",EDGE,"E428"),sQuery(id+"F0.wireOp",EDGE,"E429"),sQuery(id+"F0.wireOp",EDGE,"E430"),sQuery(id+"F0.wireOp",EDGE,"E431"),sQuery(id+"F0.wireOp",EDGE,"E432"),sQuery(id+"F0.wireOp",EDGE,"E433"),sQuery(id+"F0.wireOp",EDGE,"E434"),sQuery(id+"F0.wireOp",EDGE,"E435"),sQuery(id+"F0.wireOp",EDGE,"E436"),sQuery(id+"F0.wireOp",EDGE,"E437"),sQuery(id+"F0.wireOp",EDGE,"E438"),sQuery(id+"F0.wireOp",EDGE,"E439"),sQuery(id+"F0.wireOp",EDGE,"E440"),sQuery(id+"F0.wireOp",EDGE,"E441"),sQuery(id+"F0.wireOp",EDGE,"E442"),sQuery(id+"F0.wireOp",EDGE,"E443"),sQuery(id+"F0.wireOp",EDGE,"E444"),sQuery(id+"F0.wireOp",EDGE,"E445"),sQuery(id+"F0.wireOp",EDGE,"E446"),sQuery(id+"F0.wireOp",EDGE,"E447"),sQuery(id+"F0.wireOp",EDGE,"E448"),sQuery(id+"F0.wireOp",EDGE,"E449"),sQuery(id+"F0.wireOp",EDGE,"E450"),sQuery(id+"F0.wireOp",EDGE,"E451"),sQuery(id+"F0.wireOp",EDGE,"E452"),sQuery(id+"F0.wireOp",EDGE,"E453"),sQuery(id+"F0.wireOp",EDGE,"E454"),sQuery(id+"F0.wireOp",EDGE,"E455"),sQuery(id+"F0.wireOp",EDGE,"E456"),sQuery(id+"F0.wireOp",EDGE,"E457"),sQuery(id+"F0.wireOp",EDGE,"E458"),sQuery(id+"F0.wireOp",EDGE,"E459"),sQuery(id+"F0.wireOp",EDGE,"E460"),sQuery(id+"F0.wireOp",EDGE,"E461"),sQuery(id+"F0.wireOp",EDGE,"E462"),sQuery(id+"F0.wireOp",EDGE,"E463"),sQuery(id+"F0.wireOp",EDGE,"E464"),sQuery(id+"F0.wireOp",EDGE,"E465"),sQuery(id+"F0.wireOp",EDGE,"E466"),sQuery(id+"F0.wireOp",EDGE,"E467"),sQuery(id+"F0.wireOp",EDGE,"E468"),sQuery(id+"F0.wireOp",EDGE,"E469"),sQuery(id+"F0.wireOp",EDGE,"E470"),sQuery(id+"F0.wireOp",EDGE,"E471"),sQuery(id+"F0.wireOp",EDGE,"E473"),sQuery(id+"F0.wireOp",EDGE,"E474"),sQuery(id+"F0.wireOp",EDGE,"E475"),sQuery(id+"F0.wireOp",EDGE,"E476"),sQuery(id+"F0.wireOp",EDGE,"E477"),sQuery(id+"F0.wireOp",EDGE,"E478"),sQuery(id+"F0.wireOp",EDGE,"E479"),sQuery(id+"F0.wireOp",EDGE,"E480"),sQuery(id+"F0.wireOp",EDGE,"E481"),sQuery(id+"F0.wireOp",EDGE,"E482"),sQuery(id+"F0.wireOp",EDGE,"E483"),sQuery(id+"F0.wireOp",EDGE,"E484"),sQuery(id+"F0.wireOp",EDGE,"E485"),sQuery(id+"F0.wireOp",EDGE,"E486"),sQuery(id+"F0.wireOp",EDGE,"E487"),sQuery(id+"F0.wireOp",EDGE,"E488"),sQuery(id+"F0.wireOp",EDGE,"E489"),sQuery(id+"F0.wireOp",EDGE,"E490"),sQuery(id+"F0.wireOp",EDGE,"E491"),sQuery(id+"F0.wireOp",EDGE,"E492"),sQuery(id+"F0.wireOp",EDGE,"E493"),sQuery(id+"F0.wireOp",EDGE,"E494"),sQuery(id+"F0.wireOp",EDGE,"E495"),sQuery(id+"F0.wireOp",EDGE,"E496"),sQuery(id+"F0.wireOp",EDGE,"E497"),sQuery(id+"F0.wireOp",EDGE,"E498"),sQuery(id+"F0.wireOp",EDGE,"E499"),sQuery(id+"F0.wireOp",EDGE,"E500"),sQuery(id+"F0.wireOp",EDGE,"E501"),sQuery(id+"F0.wireOp",EDGE,"E502"),sQuery(id+"F0.wireOp",EDGE,"E503")])]});
            var Q1;
            Q1=makeQuery(id+"F1.opExtrude","CAP_VERTEX",VERTEX,{"disambiguationData":[OSD([sQuery(id+"F0.wireOp",EDGE,"E5"),sQuery(id+"F0.wireOp",EDGE,"E6")])],"isStart":false});
            transform(context, id + "F2", {"entities" : qUnion([Q0]), "transformType" : TransformType.SCALE_UNIFORMLY, "scale" : 0.85, "scalePoint" : qUnion([Q1]), "makeCopy" : false});
        }
    });
